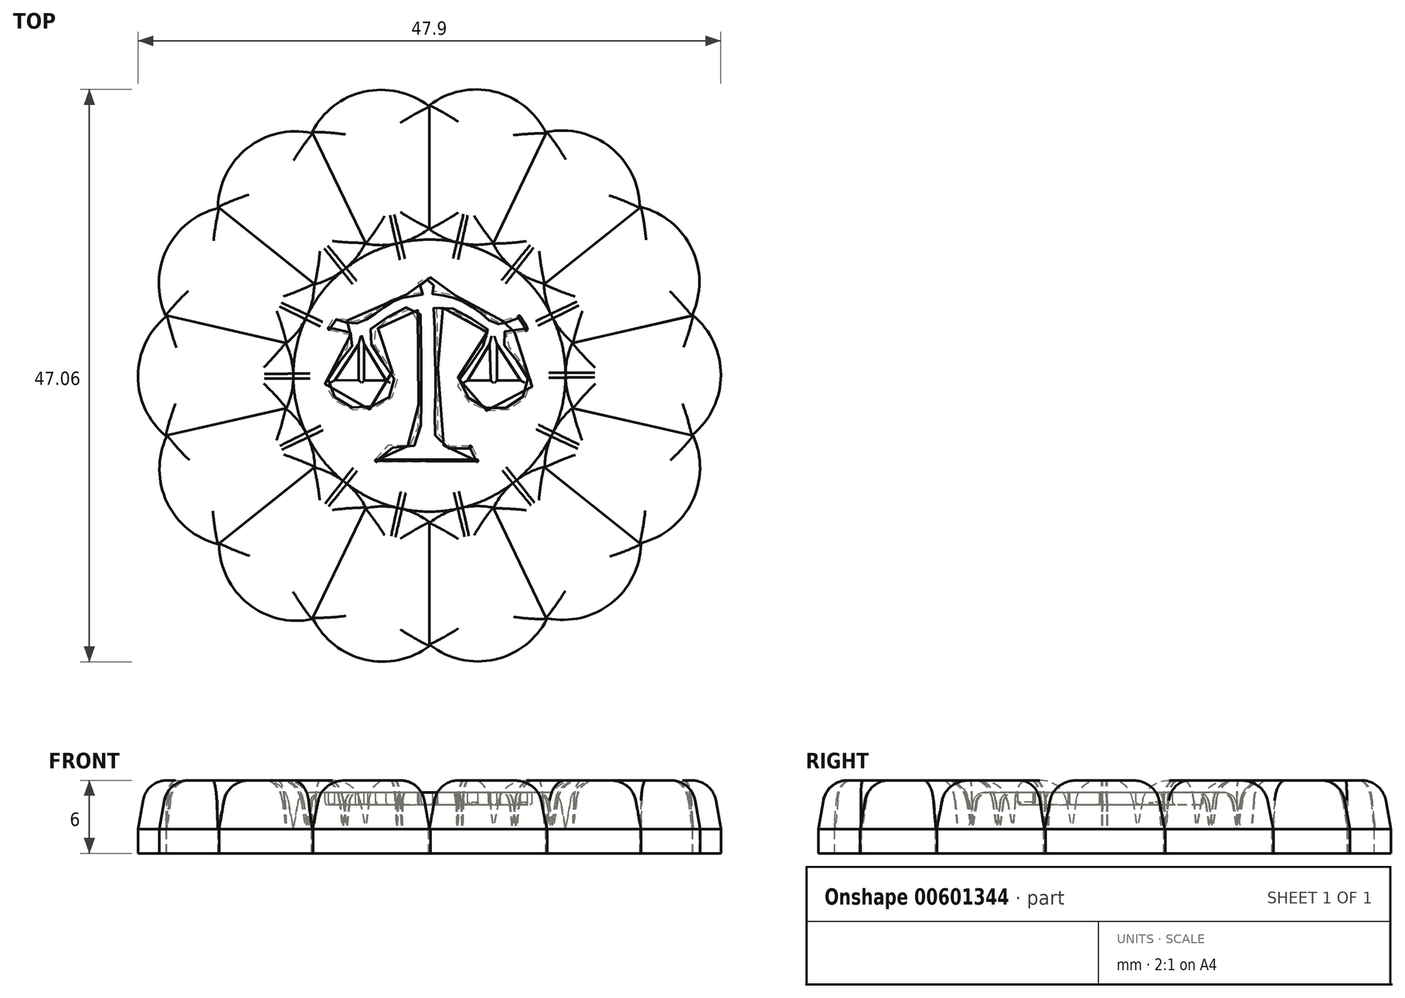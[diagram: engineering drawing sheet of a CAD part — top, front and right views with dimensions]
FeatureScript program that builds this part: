
annotation { "Feature Type Name" : "Feature", "Feature Type Description" : "" }
export const myFeature = defineFeature(function(context is Context, id is Id, definition is map)
    precondition{}
    {
        {
            var Q0;
            Q0=qCreatedBy(makeId("Top.planeOp"),FACE);
            var sketch = newSketch(context, id + "F0", { "sketchPlane" : qUnion([Q0])});
            skCircle(sketch, "E0", {"center": v(0, 0) * mm, "radius": 11.19 * mm});
            skLineSegment(sketch, "E1", {"start": v(0, 11.19) * mm, "end": v(0, 22.24) * mm});
            skLineSegment(sketch, "E2", {"start": v(4.86, 10.08) * mm, "end": v(9.6, 19.92) * mm});
            skArc(sketch, "E3", {"start": v(-0.04, 12.08) * mm, "mid": v(2.48, 10.9) * mm, "end": v(5.26, 10.91) * mm});
            skPoint(sketch, "E3.third.point", {"position": v(2.25, 10.96) * mm});
            skArc(sketch, "E4.1.0", {"start": v(-5.28, 10.86) * mm, "mid": v(-2.5, 10.9) * mm, "end": v(0, 12.11) * mm});
            skLineSegment(sketch, "E4.1.1", {"start": v(0, 11.19) * mm, "end": v(0, 22.11) * mm});
            skLineSegment(sketch, "E4.1.2", {"start": v(-4.85, 10.08) * mm, "end": v(-9.65, 20.03) * mm});
            skArc(sketch, "E4.2.0", {"start": v(-9.6, 19.92) * mm, "mid": v(-14.96, 18.7) * mm, "end": v(-17.39, 13.76) * mm});
            skLineSegment(sketch, "E4.2.1", {"start": v(-4.85, 10.08) * mm, "end": v(-9.6, 19.92) * mm});
            skLineSegment(sketch, "E4.2.2", {"start": v(-8.75, 6.98) * mm, "end": v(-17.39, 13.86) * mm});
            skArc(sketch, "E4.3.0", {"start": v(-11.79, 2.65) * mm, "mid": v(-10.08, 4.84) * mm, "end": v(-9.47, 7.55) * mm});
            skLineSegment(sketch, "E4.3.1", {"start": v(-8.75, 6.98) * mm, "end": v(-17.29, 13.79) * mm});
            skLineSegment(sketch, "E4.3.2", {"start": v(-10.9, 2.49) * mm, "end": v(-21.68, 4.95) * mm});
            skArc(sketch, "E4.4.0", {"start": v(-11.77, -2.73) * mm, "mid": v(-11.18, -0.01) * mm, "end": v(-11.81, 2.7) * mm});
            skLineSegment(sketch, "E4.4.1", {"start": v(-10.9, 2.5) * mm, "end": v(-21.56, 4.92) * mm});
            skLineSegment(sketch, "E4.4.2", {"start": v(-10.9, -2.49) * mm, "end": v(-21.68, -4.95) * mm});
            skArc(sketch, "E4.5.0", {"start": v(-9.42, -7.57) * mm, "mid": v(-10.07, -4.86) * mm, "end": v(-11.81, -2.7) * mm});
            skLineSegment(sketch, "E4.5.1", {"start": v(-10.9, -2.49) * mm, "end": v(-21.56, -4.92) * mm});
            skLineSegment(sketch, "E4.5.2", {"start": v(-8.75, -6.98) * mm, "end": v(-17.39, -13.86) * mm});
            skArc(sketch, "E4.6.0", {"start": v(-5.2, -10.9) * mm, "mid": v(-6.96, -8.75) * mm, "end": v(-9.47, -7.55) * mm});
            skLineSegment(sketch, "E4.6.1", {"start": v(-8.75, -6.97) * mm, "end": v(-17.29, -13.78) * mm});
            skLineSegment(sketch, "E4.6.2", {"start": v(-4.85, -10.08) * mm, "end": v(-9.65, -20.03) * mm});
            skArc(sketch, "E4.7.0", {"start": v(0.04, -12.08) * mm, "mid": v(-2.48, -10.9) * mm, "end": v(-5.26, -10.91) * mm});
            skLineSegment(sketch, "E4.7.1", {"start": v(-4.86, -10.08) * mm, "end": v(-9.6, -19.92) * mm});
            skLineSegment(sketch, "E4.7.2", {"start": v(0, -11.19) * mm, "end": v(0, -22.24) * mm});
            skArc(sketch, "E4.8.0", {"start": v(5.28, -10.86) * mm, "mid": v(2.5, -10.9) * mm, "end": v(0, -12.11) * mm});
            skLineSegment(sketch, "E4.8.1", {"start": v(0, -11.19) * mm, "end": v(0, -22.11) * mm});
            skLineSegment(sketch, "E4.8.2", {"start": v(4.85, -10.08) * mm, "end": v(9.65, -20.03) * mm});
            skArc(sketch, "E4.9.0", {"start": v(9.47, -7.5) * mm, "mid": v(6.98, -8.74) * mm, "end": v(5.26, -10.92) * mm});
            skLineSegment(sketch, "E4.9.1", {"start": v(4.85, -10.08) * mm, "end": v(9.6, -19.92) * mm});
            skLineSegment(sketch, "E4.9.2", {"start": v(9.42, -7.51) * mm, "end": v(17.39, -13.86) * mm});
            skArc(sketch, "E4.10.0", {"start": v(11.79, -2.65) * mm, "mid": v(10.08, -4.84) * mm, "end": v(9.47, -7.55) * mm});
            skLineSegment(sketch, "E4.10.1", {"start": v(8.75, -6.98) * mm, "end": v(17.29, -13.79) * mm});
            skLineSegment(sketch, "E4.10.2", {"start": v(10.9, -2.49) * mm, "end": v(21.68, -4.95) * mm});
            skArc(sketch, "E4.11.0", {"start": v(11.77, 2.73) * mm, "mid": v(11.18, 0.01) * mm, "end": v(11.81, -2.7) * mm});
            skLineSegment(sketch, "E4.11.1", {"start": v(10.9, -2.5) * mm, "end": v(21.56, -4.92) * mm});
            skLineSegment(sketch, "E4.11.2", {"start": v(10.9, 2.49) * mm, "end": v(21.68, 4.95) * mm});
            skArc(sketch, "E4.12.0", {"start": v(9.42, 7.57) * mm, "mid": v(10.07, 4.86) * mm, "end": v(11.81, 2.7) * mm});
            skLineSegment(sketch, "E4.12.1", {"start": v(10.9, 2.49) * mm, "end": v(21.56, 4.92) * mm});
            skLineSegment(sketch, "E4.12.2", {"start": v(8.75, 6.98) * mm, "end": v(17.39, 13.86) * mm});
            skArc(sketch, "E4.13.0", {"start": v(5.2, 10.9) * mm, "mid": v(6.96, 8.75) * mm, "end": v(9.47, 7.55) * mm});
            skLineSegment(sketch, "E4.13.1", {"start": v(8.75, 6.97) * mm, "end": v(17.29, 13.78) * mm});
            skLineSegment(sketch, "E4.13.2", {"start": v(4.85, 10.08) * mm, "end": v(9.65, 20.03) * mm});
            skArc(sketch, "E5.trimOffspring", {"start": v(0, 22.11) * mm, "mid": v(-5.36, 23.34) * mm, "end": v(-9.7, 19.95) * mm});
            skArc(sketch, "E6.trimOffspring", {"start": v(9.6, 19.92) * mm, "mid": v(5.3, 23.36) * mm, "end": v(-0.08, 22.18) * mm});
            skArc(sketch, "E7.trimOffspring", {"start": v(17.29, 13.78) * mm, "mid": v(14.9, 18.75) * mm, "end": v(9.55, 20.01) * mm});
            skArc(sketch, "E8.trimOffspring", {"start": v(21.56, 4.92) * mm, "mid": v(21.57, 10.42) * mm, "end": v(17.29, 13.89) * mm});
            skArc(sketch, "E9.trimOffspring", {"start": v(21.56, -4.92) * mm, "mid": v(23.95, 0.03) * mm, "end": v(21.6, 5.01) * mm});
            skArc(sketch, "E10.trimOffspring", {"start": v(17.29, -13.79) * mm, "mid": v(21.6, -10.36) * mm, "end": v(21.64, -4.86) * mm});
            skArc(sketch, "E11.trimOffspring", {"start": v(9.6, -19.92) * mm, "mid": v(14.96, -18.7) * mm, "end": v(17.39, -13.76) * mm});
            skArc(sketch, "E12.trimOffspring", {"start": v(0, -22.11) * mm, "mid": v(5.36, -23.34) * mm, "end": v(9.7, -19.95) * mm});
            skArc(sketch, "E13.trimOffspring", {"start": v(-9.6, -19.92) * mm, "mid": v(-5.3, -23.36) * mm, "end": v(0.08, -22.18) * mm});
            skArc(sketch, "E14.trimOffspring", {"start": v(-17.29, -13.78) * mm, "mid": v(-14.9, -18.75) * mm, "end": v(-9.55, -20.01) * mm});
            skArc(sketch, "E15.trimOffspring", {"start": v(-21.56, -4.92) * mm, "mid": v(-21.57, -10.42) * mm, "end": v(-17.29, -13.89) * mm});
            skArc(sketch, "E16.trimOffspring", {"start": v(-21.56, 4.92) * mm, "mid": v(-23.95, -0.03) * mm, "end": v(-21.6, -5.01) * mm});
            skArc(sketch, "E17.trimOffspring", {"start": v(-9.47, 7.5) * mm, "mid": v(-6.98, 8.74) * mm, "end": v(-5.26, 10.92) * mm});
            skArc(sketch, "E18.trimOffspring", {"start": v(-17.29, 13.79) * mm, "mid": v(-21.6, 10.36) * mm, "end": v(-21.64, 4.86) * mm});
            skSolve(sketch);
        }
        {
            var Q0;
            {var subQ0=sQuery(id+"F0.wireOp",EDGE,"E17.trimOffspring");var subQ2=sQuery(id+"F0.wireOp",EDGE,"E0");var subQ3=makeQuery(id+"F0.imprint","INTERSECT",VERTEX,{"disambiguationData":[OD(0.0)],"derivedFrom":[subQ2,subQ0]});Q0=makeQuery(id+"F0.imprint","IMPRINT",FACE,{"disambiguationData":[TD([[makeQuery(id+"F0.imprint","IMPRINT",EDGE,{"disambiguationData":[TD([[subQ3,-1.0]])],"derivedFrom":subQ2}),-1.0]])]});}
            var Q1;
            {var subQ4=sQuery(id+"F0.wireOp",EDGE,"E4.1.0");var subQ15=sQuery(id+"F0.wireOp",EDGE,"E0");var subQ16=makeQuery(id+"F0.imprint","INTERSECT",VERTEX,{"disambiguationData":[OD(0.0)],"derivedFrom":[subQ15,subQ4]});Q1=makeQuery(id+"F0.imprint","IMPRINT",FACE,{"disambiguationData":[TD([[makeQuery(id+"F0.imprint","IMPRINT",EDGE,{"disambiguationData":[TD([[subQ16,-1.0]])],"derivedFrom":subQ15}),-1.0]])]});}
            var Q2;
            {var subQ10=sQuery(id+"F0.wireOp",EDGE,"E3");var subQ14=sQuery(id+"F0.wireOp",EDGE,"E0");var subQ15=makeQuery(id+"F0.imprint","INTERSECT",VERTEX,{"disambiguationData":[OD(0.0)],"derivedFrom":[subQ14,subQ10]});Q2=makeQuery(id+"F0.imprint","IMPRINT",FACE,{"disambiguationData":[TD([[makeQuery(id+"F0.imprint","IMPRINT",EDGE,{"disambiguationData":[TD([[subQ15,-1.0]])],"derivedFrom":subQ14}),-1.0]])]});}
            var Q3;
            {var subQ10=sQuery(id+"F0.wireOp",EDGE,"E4.13.0");var subQ11=sQuery(id+"F0.wireOp",EDGE,"E0");var subQ16=makeQuery(id+"F0.imprint","INTERSECT",VERTEX,{"disambiguationData":[OD(0.0)],"derivedFrom":[subQ11,subQ10]});Q3=makeQuery(id+"F0.imprint","IMPRINT",FACE,{"disambiguationData":[TD([[makeQuery(id+"F0.imprint","IMPRINT",EDGE,{"disambiguationData":[TD([[subQ16,-1.0]])],"derivedFrom":subQ11}),-1.0]])]});}
            var Q4;
            {var subQ11=sQuery(id+"F0.wireOp",EDGE,"E4.12.0");var subQ15=sQuery(id+"F0.wireOp",EDGE,"E0");var subQ16=makeQuery(id+"F0.imprint","INTERSECT",VERTEX,{"disambiguationData":[OD(0.0)],"derivedFrom":[subQ15,subQ11]});Q4=makeQuery(id+"F0.imprint","IMPRINT",FACE,{"disambiguationData":[TD([[makeQuery(id+"F0.imprint","IMPRINT",EDGE,{"disambiguationData":[TD([[subQ16,-1.0]])],"derivedFrom":subQ15}),-1.0]])]});}
            var Q5;
            {var subQ6=sQuery(id+"F0.wireOp",EDGE,"E4.11.0");var subQ11=sQuery(id+"F0.wireOp",EDGE,"E0");var subQ12=makeQuery(id+"F0.imprint","INTERSECT",VERTEX,{"disambiguationData":[OD(0.0)],"derivedFrom":[subQ11,subQ6]});Q5=makeQuery(id+"F0.imprint","IMPRINT",FACE,{"disambiguationData":[TD([[makeQuery(id+"F0.imprint","IMPRINT",EDGE,{"disambiguationData":[TD([[subQ12,1.0]])],"derivedFrom":subQ11}),-1.0]])]});}
            var Q6;
            {var subQ10=sQuery(id+"F0.wireOp",EDGE,"E4.10.0");var subQ14=sQuery(id+"F0.wireOp",EDGE,"E0");var subQ15=makeQuery(id+"F0.imprint","INTERSECT",VERTEX,{"disambiguationData":[OD(0.0)],"derivedFrom":[subQ14,subQ10]});Q6=makeQuery(id+"F0.imprint","IMPRINT",FACE,{"disambiguationData":[TD([[makeQuery(id+"F0.imprint","IMPRINT",EDGE,{"disambiguationData":[TD([[subQ15,-1.0]])],"derivedFrom":subQ14}),-1.0]])]});}
            var Q7;
            {var subQ4=sQuery(id+"F0.wireOp",EDGE,"E4.9.0");var subQ5=sQuery(id+"F0.wireOp",EDGE,"E0");var subQ17=makeQuery(id+"F0.imprint","INTERSECT",VERTEX,{"disambiguationData":[OD(0.0)],"derivedFrom":[subQ5,subQ4]});Q7=makeQuery(id+"F0.imprint","IMPRINT",FACE,{"disambiguationData":[TD([[makeQuery(id+"F0.imprint","IMPRINT",EDGE,{"disambiguationData":[TD([[subQ17,-1.0]])],"derivedFrom":subQ5}),-1.0]])]});}
            var Q8;
            {var subQ6=sQuery(id+"F0.wireOp",EDGE,"E4.8.0");var subQ11=sQuery(id+"F0.wireOp",EDGE,"E0");var subQ12=makeQuery(id+"F0.imprint","INTERSECT",VERTEX,{"disambiguationData":[OD(0.0)],"derivedFrom":[subQ11,subQ6]});Q8=makeQuery(id+"F0.imprint","IMPRINT",FACE,{"disambiguationData":[TD([[makeQuery(id+"F0.imprint","IMPRINT",EDGE,{"disambiguationData":[TD([[subQ12,-1.0]])],"derivedFrom":subQ11}),-1.0]])]});}
            var Q9;
            {var subQ4=sQuery(id+"F0.wireOp",EDGE,"E4.7.0");var subQ9=sQuery(id+"F0.wireOp",EDGE,"E0");var subQ10=makeQuery(id+"F0.imprint","INTERSECT",VERTEX,{"disambiguationData":[OD(0.0)],"derivedFrom":[subQ9,subQ4]});Q9=makeQuery(id+"F0.imprint","IMPRINT",FACE,{"disambiguationData":[TD([[makeQuery(id+"F0.imprint","IMPRINT",EDGE,{"disambiguationData":[TD([[subQ10,-1.0]])],"derivedFrom":subQ9}),-1.0]])]});}
            var Q10;
            {var subQ6=sQuery(id+"F0.wireOp",EDGE,"E4.6.0");var subQ14=sQuery(id+"F0.wireOp",EDGE,"E0");var subQ15=makeQuery(id+"F0.imprint","INTERSECT",VERTEX,{"disambiguationData":[OD(0.0)],"derivedFrom":[subQ14,subQ6]});Q10=makeQuery(id+"F0.imprint","IMPRINT",FACE,{"disambiguationData":[TD([[makeQuery(id+"F0.imprint","IMPRINT",EDGE,{"disambiguationData":[TD([[subQ15,-1.0]])],"derivedFrom":subQ14}),-1.0]])]});}
            var Q11;
            {var subQ10=sQuery(id+"F0.wireOp",EDGE,"E4.5.0");var subQ14=sQuery(id+"F0.wireOp",EDGE,"E0");var subQ15=makeQuery(id+"F0.imprint","INTERSECT",VERTEX,{"disambiguationData":[OD(0.0)],"derivedFrom":[subQ14,subQ10]});Q11=makeQuery(id+"F0.imprint","IMPRINT",FACE,{"disambiguationData":[TD([[makeQuery(id+"F0.imprint","IMPRINT",EDGE,{"disambiguationData":[TD([[subQ15,-1.0]])],"derivedFrom":subQ14}),-1.0]])]});}
            var Q12;
            {var subQ10=sQuery(id+"F0.wireOp",EDGE,"E4.4.0");var subQ14=sQuery(id+"F0.wireOp",EDGE,"E0");var subQ15=makeQuery(id+"F0.imprint","INTERSECT",VERTEX,{"disambiguationData":[OD(0.0)],"derivedFrom":[subQ14,subQ10]});Q12=makeQuery(id+"F0.imprint","IMPRINT",FACE,{"disambiguationData":[TD([[makeQuery(id+"F0.imprint","IMPRINT",EDGE,{"disambiguationData":[TD([[subQ15,-1.0]])],"derivedFrom":subQ14}),-1.0]])]});}
            var Q13;
            {var subQ11=sQuery(id+"F0.wireOp",EDGE,"E4.3.0");var subQ12=sQuery(id+"F0.wireOp",EDGE,"E0");var subQ17=makeQuery(id+"F0.imprint","INTERSECT",VERTEX,{"disambiguationData":[OD(0.0)],"derivedFrom":[subQ12,subQ11]});Q13=makeQuery(id+"F0.imprint","IMPRINT",FACE,{"disambiguationData":[TD([[makeQuery(id+"F0.imprint","IMPRINT",EDGE,{"disambiguationData":[TD([[subQ17,-1.0]])],"derivedFrom":subQ12}),-1.0]])]});}
            extrude(context, id + "F1", {"entities" : qUnion([Q0, Q1, Q2, Q3, Q4, Q5, Q6, Q7, Q8, Q9, Q10, Q11, Q12, Q13]), "depth" : 4 * mm, "offsetDistance" : 25 * mm, "hasDraft" : true, "draftAngle" : 10 * degree, "draftPullDirection" : true});
        }
        {
            var Q0;
            {var subQ1=sQuery(id+"F0.wireOp",EDGE,"E0");var subQ13=makeQuery(id+"F0.imprint","INTERSECT",VERTEX,{"derivedFrom":[subQ1,sQuery(id+"F0.wireOp",EDGE,"E4.12.1")]});Q0=makeQuery(id+"F0.imprint","IMPRINT",FACE,{"disambiguationData":[TD([[makeQuery(id+"F0.imprint","IMPRINT",EDGE,{"disambiguationData":[TD([[subQ13,1.0]])],"derivedFrom":subQ1}),1.0]])]});}
            extrude(context, id + "F2", {"entities" : qUnion([Q0]), "depth" : 3 * mm, "offsetDistance" : 25 * mm, "hasDraft" : true, "draftAngle" : 10 * degree, "draftPullDirection" : true});
        }
        {
            var Q0;
            {var subQ10=sQuery(id+"F0.wireOp",EDGE,"E4.5.0");var subQ14=sQuery(id+"F0.wireOp",EDGE,"E0");var subQ15=makeQuery(id+"F0.imprint","INTERSECT",VERTEX,{"disambiguationData":[OD(0.0)],"derivedFrom":[subQ14,subQ10]});Q0=makeQuery(id+"F0.imprint","IMPRINT",FACE,{"disambiguationData":[TD([[makeQuery(id+"F0.imprint","IMPRINT",EDGE,{"disambiguationData":[TD([[subQ15,-1.0]])],"derivedFrom":subQ14}),-1.0]])]});}
            var Q1;
            {var subQ6=sQuery(id+"F0.wireOp",EDGE,"E4.11.0");var subQ11=sQuery(id+"F0.wireOp",EDGE,"E0");var subQ12=makeQuery(id+"F0.imprint","INTERSECT",VERTEX,{"disambiguationData":[OD(0.0)],"derivedFrom":[subQ11,subQ6]});Q1=makeQuery(id+"F0.imprint","IMPRINT",FACE,{"disambiguationData":[TD([[makeQuery(id+"F0.imprint","IMPRINT",EDGE,{"disambiguationData":[TD([[subQ12,1.0]])],"derivedFrom":subQ11}),-1.0]])]});}
            var Q2;
            {var subQ10=sQuery(id+"F0.wireOp",EDGE,"E4.10.0");var subQ14=sQuery(id+"F0.wireOp",EDGE,"E0");var subQ15=makeQuery(id+"F0.imprint","INTERSECT",VERTEX,{"disambiguationData":[OD(0.0)],"derivedFrom":[subQ14,subQ10]});Q2=makeQuery(id+"F0.imprint","IMPRINT",FACE,{"disambiguationData":[TD([[makeQuery(id+"F0.imprint","IMPRINT",EDGE,{"disambiguationData":[TD([[subQ15,-1.0]])],"derivedFrom":subQ14}),-1.0]])]});}
            var Q3;
            {var subQ10=sQuery(id+"F0.wireOp",EDGE,"E4.4.0");var subQ14=sQuery(id+"F0.wireOp",EDGE,"E0");var subQ15=makeQuery(id+"F0.imprint","INTERSECT",VERTEX,{"disambiguationData":[OD(0.0)],"derivedFrom":[subQ14,subQ10]});Q3=makeQuery(id+"F0.imprint","IMPRINT",FACE,{"disambiguationData":[TD([[makeQuery(id+"F0.imprint","IMPRINT",EDGE,{"disambiguationData":[TD([[subQ15,-1.0]])],"derivedFrom":subQ14}),-1.0]])]});}
            var Q4;
            {var subQ11=sQuery(id+"F0.wireOp",EDGE,"E4.3.0");var subQ12=sQuery(id+"F0.wireOp",EDGE,"E0");var subQ17=makeQuery(id+"F0.imprint","INTERSECT",VERTEX,{"disambiguationData":[OD(0.0)],"derivedFrom":[subQ12,subQ11]});Q4=makeQuery(id+"F0.imprint","IMPRINT",FACE,{"disambiguationData":[TD([[makeQuery(id+"F0.imprint","IMPRINT",EDGE,{"disambiguationData":[TD([[subQ17,-1.0]])],"derivedFrom":subQ12}),-1.0]])]});}
            var Q5;
            {var subQ1=sQuery(id+"F0.wireOp",EDGE,"E0");var subQ13=makeQuery(id+"F0.imprint","INTERSECT",VERTEX,{"derivedFrom":[subQ1,sQuery(id+"F0.wireOp",EDGE,"E4.12.1")]});Q5=makeQuery(id+"F0.imprint","IMPRINT",FACE,{"disambiguationData":[TD([[makeQuery(id+"F0.imprint","IMPRINT",EDGE,{"disambiguationData":[TD([[subQ13,1.0]])],"derivedFrom":subQ1}),1.0]])]});}
            var Q6;
            {var subQ4=sQuery(id+"F0.wireOp",EDGE,"E4.9.0");var subQ5=sQuery(id+"F0.wireOp",EDGE,"E0");var subQ17=makeQuery(id+"F0.imprint","INTERSECT",VERTEX,{"disambiguationData":[OD(0.0)],"derivedFrom":[subQ5,subQ4]});Q6=makeQuery(id+"F0.imprint","IMPRINT",FACE,{"disambiguationData":[TD([[makeQuery(id+"F0.imprint","IMPRINT",EDGE,{"disambiguationData":[TD([[subQ17,-1.0]])],"derivedFrom":subQ5}),-1.0]])]});}
            var Q7;
            {var subQ0=sQuery(id+"F0.wireOp",EDGE,"E17.trimOffspring");var subQ2=sQuery(id+"F0.wireOp",EDGE,"E0");var subQ3=makeQuery(id+"F0.imprint","INTERSECT",VERTEX,{"disambiguationData":[OD(0.0)],"derivedFrom":[subQ2,subQ0]});Q7=makeQuery(id+"F0.imprint","IMPRINT",FACE,{"disambiguationData":[TD([[makeQuery(id+"F0.imprint","IMPRINT",EDGE,{"disambiguationData":[TD([[subQ3,-1.0]])],"derivedFrom":subQ2}),-1.0]])]});}
            var Q8;
            {var subQ10=sQuery(id+"F0.wireOp",EDGE,"E4.13.0");var subQ11=sQuery(id+"F0.wireOp",EDGE,"E0");var subQ16=makeQuery(id+"F0.imprint","INTERSECT",VERTEX,{"disambiguationData":[OD(0.0)],"derivedFrom":[subQ11,subQ10]});Q8=makeQuery(id+"F0.imprint","IMPRINT",FACE,{"disambiguationData":[TD([[makeQuery(id+"F0.imprint","IMPRINT",EDGE,{"disambiguationData":[TD([[subQ16,-1.0]])],"derivedFrom":subQ11}),-1.0]])]});}
            var Q9;
            {var subQ6=sQuery(id+"F0.wireOp",EDGE,"E4.6.0");var subQ14=sQuery(id+"F0.wireOp",EDGE,"E0");var subQ15=makeQuery(id+"F0.imprint","INTERSECT",VERTEX,{"disambiguationData":[OD(0.0)],"derivedFrom":[subQ14,subQ6]});Q9=makeQuery(id+"F0.imprint","IMPRINT",FACE,{"disambiguationData":[TD([[makeQuery(id+"F0.imprint","IMPRINT",EDGE,{"disambiguationData":[TD([[subQ15,-1.0]])],"derivedFrom":subQ14}),-1.0]])]});}
            var Q10;
            {var subQ10=sQuery(id+"F0.wireOp",EDGE,"E3");var subQ14=sQuery(id+"F0.wireOp",EDGE,"E0");var subQ15=makeQuery(id+"F0.imprint","INTERSECT",VERTEX,{"disambiguationData":[OD(0.0)],"derivedFrom":[subQ14,subQ10]});Q10=makeQuery(id+"F0.imprint","IMPRINT",FACE,{"disambiguationData":[TD([[makeQuery(id+"F0.imprint","IMPRINT",EDGE,{"disambiguationData":[TD([[subQ15,-1.0]])],"derivedFrom":subQ14}),-1.0]])]});}
            var Q11;
            {var subQ4=sQuery(id+"F0.wireOp",EDGE,"E4.7.0");var subQ9=sQuery(id+"F0.wireOp",EDGE,"E0");var subQ10=makeQuery(id+"F0.imprint","INTERSECT",VERTEX,{"disambiguationData":[OD(0.0)],"derivedFrom":[subQ9,subQ4]});Q11=makeQuery(id+"F0.imprint","IMPRINT",FACE,{"disambiguationData":[TD([[makeQuery(id+"F0.imprint","IMPRINT",EDGE,{"disambiguationData":[TD([[subQ10,-1.0]])],"derivedFrom":subQ9}),-1.0]])]});}
            var Q12;
            {var subQ4=sQuery(id+"F0.wireOp",EDGE,"E4.1.0");var subQ15=sQuery(id+"F0.wireOp",EDGE,"E0");var subQ16=makeQuery(id+"F0.imprint","INTERSECT",VERTEX,{"disambiguationData":[OD(0.0)],"derivedFrom":[subQ15,subQ4]});Q12=makeQuery(id+"F0.imprint","IMPRINT",FACE,{"disambiguationData":[TD([[makeQuery(id+"F0.imprint","IMPRINT",EDGE,{"disambiguationData":[TD([[subQ16,-1.0]])],"derivedFrom":subQ15}),-1.0]])]});}
            var Q13;
            {var subQ6=sQuery(id+"F0.wireOp",EDGE,"E4.8.0");var subQ11=sQuery(id+"F0.wireOp",EDGE,"E0");var subQ12=makeQuery(id+"F0.imprint","INTERSECT",VERTEX,{"disambiguationData":[OD(0.0)],"derivedFrom":[subQ11,subQ6]});Q13=makeQuery(id+"F0.imprint","IMPRINT",FACE,{"disambiguationData":[TD([[makeQuery(id+"F0.imprint","IMPRINT",EDGE,{"disambiguationData":[TD([[subQ12,-1.0]])],"derivedFrom":subQ11}),-1.0]])]});}
            var Q14;
            {var subQ11=sQuery(id+"F0.wireOp",EDGE,"E4.12.0");var subQ15=sQuery(id+"F0.wireOp",EDGE,"E0");var subQ16=makeQuery(id+"F0.imprint","INTERSECT",VERTEX,{"disambiguationData":[OD(0.0)],"derivedFrom":[subQ15,subQ11]});Q14=makeQuery(id+"F0.imprint","IMPRINT",FACE,{"disambiguationData":[TD([[makeQuery(id+"F0.imprint","IMPRINT",EDGE,{"disambiguationData":[TD([[subQ16,-1.0]])],"derivedFrom":subQ15}),-1.0]])]});}
            var Q15;
            {var subQ0=sQuery(id+"F0.wireOp",EDGE,"E4.11.0");var subQ1=sQuery(id+"F0.wireOp",EDGE,"E0");var subQ2=makeQuery(id+"F0.imprint","INTERSECT",VERTEX,{"disambiguationData":[OD(0.0)],"derivedFrom":[subQ1,subQ0]});Q15=makeQuery(id+"F0.imprint","IMPRINT",FACE,{"disambiguationData":[TD([[makeQuery(id+"F0.imprint","IMPRINT",EDGE,{"disambiguationData":[TD([[subQ2,1.0]])],"derivedFrom":subQ1}),1.0]])]});}
            var Q16;
            {var subQ0=sQuery(id+"F0.wireOp",EDGE,"E4.8.1");var subQ1=sQuery(id+"F0.wireOp",EDGE,"E0");var subQ2=makeQuery(id+"F0.imprint","INTERSECT",VERTEX,{"derivedFrom":[subQ1,subQ0]});Q16=makeQuery(id+"F0.imprint","IMPRINT",FACE,{"disambiguationData":[TD([[makeQuery(id+"F0.imprint","IMPRINT",EDGE,{"disambiguationData":[TD([[subQ2,1.0]])],"derivedFrom":subQ1}),-1.0]])]});}
            var Q17;
            {var subQ0=sQuery(id+"F0.wireOp",EDGE,"E4.7.1");var subQ1=sQuery(id+"F0.wireOp",EDGE,"E0");var subQ2=makeQuery(id+"F0.imprint","INTERSECT",VERTEX,{"derivedFrom":[subQ1,subQ0]});Q17=makeQuery(id+"F0.imprint","IMPRINT",FACE,{"disambiguationData":[TD([[makeQuery(id+"F0.imprint","IMPRINT",EDGE,{"disambiguationData":[TD([[subQ2,1.0]])],"derivedFrom":subQ1}),-1.0]])]});}
            var Q18;
            {var subQ0=sQuery(id+"F0.wireOp",EDGE,"E4.13.2");var subQ1=sQuery(id+"F0.wireOp",EDGE,"E0");var subQ2=makeQuery(id+"F0.imprint","INTERSECT",VERTEX,{"derivedFrom":[subQ1,subQ0]});Q18=makeQuery(id+"F0.imprint","IMPRINT",FACE,{"disambiguationData":[TD([[makeQuery(id+"F0.imprint","IMPRINT",EDGE,{"disambiguationData":[TD([[subQ2,-1.0]])],"derivedFrom":subQ1}),-1.0]])]});}
            var Q19;
            {var subQ0=sQuery(id+"F0.wireOp",EDGE,"E4.7.2");var subQ1=sQuery(id+"F0.wireOp",EDGE,"E0");var subQ2=makeQuery(id+"F0.imprint","INTERSECT",VERTEX,{"derivedFrom":[subQ1,subQ0]});Q19=makeQuery(id+"F0.imprint","IMPRINT",FACE,{"disambiguationData":[TD([[makeQuery(id+"F0.imprint","IMPRINT",EDGE,{"disambiguationData":[TD([[subQ2,-1.0]])],"derivedFrom":subQ1}),-1.0]])]});}
            var Q20;
            {var subQ0=sQuery(id+"F0.wireOp",EDGE,"E4.6.1");var subQ1=sQuery(id+"F0.wireOp",EDGE,"E0");var subQ2=makeQuery(id+"F0.imprint","INTERSECT",VERTEX,{"derivedFrom":[subQ1,subQ0]});Q20=makeQuery(id+"F0.imprint","IMPRINT",FACE,{"disambiguationData":[TD([[makeQuery(id+"F0.imprint","IMPRINT",EDGE,{"disambiguationData":[TD([[subQ2,1.0]])],"derivedFrom":subQ1}),-1.0]])]});}
            var Q21;
            {var subQ0=sQuery(id+"F0.wireOp",EDGE,"E1");var subQ1=sQuery(id+"F0.wireOp",EDGE,"E0");var subQ2=makeQuery(id+"F0.imprint","INTERSECT",VERTEX,{"derivedFrom":[subQ1,subQ0]});Q21=makeQuery(id+"F0.imprint","IMPRINT",FACE,{"disambiguationData":[TD([[makeQuery(id+"F0.imprint","IMPRINT",EDGE,{"disambiguationData":[TD([[subQ2,-1.0]])],"derivedFrom":subQ1}),-1.0]])]});}
            var Q22;
            {var subQ0=sQuery(id+"F0.wireOp",EDGE,"E4.12.1");var subQ1=sQuery(id+"F0.wireOp",EDGE,"E0");var subQ2=makeQuery(id+"F0.imprint","INTERSECT",VERTEX,{"derivedFrom":[subQ1,subQ0]});Q22=makeQuery(id+"F0.imprint","IMPRINT",FACE,{"disambiguationData":[TD([[makeQuery(id+"F0.imprint","IMPRINT",EDGE,{"disambiguationData":[TD([[subQ2,1.0]])],"derivedFrom":subQ1}),-1.0]])]});}
            var Q23;
            {var subQ3=sQuery(id+"F0.wireOp",EDGE,"E0");var subQ6=sQuery(id+"F0.wireOp",EDGE,"E4.10.1");var subQ8=makeQuery(id+"F0.imprint","INTERSECT",VERTEX,{"derivedFrom":[subQ3,subQ6]});Q23=makeQuery(id+"F0.imprint","IMPRINT",FACE,{"disambiguationData":[TD([[makeQuery(id+"F0.imprint","IMPRINT",EDGE,{"disambiguationData":[TD([[subQ8,-1.0]])],"derivedFrom":subQ3}),-1.0]])]});}
            var Q24;
            {var subQ0=sQuery(id+"F0.wireOp",EDGE,"E2");var subQ1=sQuery(id+"F0.wireOp",EDGE,"E0");var subQ2=makeQuery(id+"F0.imprint","INTERSECT",VERTEX,{"derivedFrom":[subQ1,subQ0]});Q24=makeQuery(id+"F0.imprint","IMPRINT",FACE,{"disambiguationData":[TD([[makeQuery(id+"F0.imprint","IMPRINT",EDGE,{"disambiguationData":[TD([[subQ2,1.0]])],"derivedFrom":subQ1}),-1.0]])]});}
            var Q25;
            {var subQ0=sQuery(id+"F0.wireOp",EDGE,"E4.4.2");var subQ1=sQuery(id+"F0.wireOp",EDGE,"E0");var subQ2=makeQuery(id+"F0.imprint","INTERSECT",VERTEX,{"derivedFrom":[subQ1,subQ0]});Q25=makeQuery(id+"F0.imprint","IMPRINT",FACE,{"disambiguationData":[TD([[makeQuery(id+"F0.imprint","IMPRINT",EDGE,{"disambiguationData":[TD([[subQ2,-1.0]])],"derivedFrom":subQ1}),-1.0]])]});}
            var Q26;
            {var subQ0=sQuery(id+"F0.wireOp",EDGE,"E4.8.2");var subQ1=sQuery(id+"F0.wireOp",EDGE,"E0");var subQ2=makeQuery(id+"F0.imprint","INTERSECT",VERTEX,{"derivedFrom":[subQ1,subQ0]});Q26=makeQuery(id+"F0.imprint","IMPRINT",FACE,{"disambiguationData":[TD([[makeQuery(id+"F0.imprint","IMPRINT",EDGE,{"disambiguationData":[TD([[subQ2,-1.0]])],"derivedFrom":subQ1}),-1.0]])]});}
            var Q27;
            {var subQ0=sQuery(id+"F0.wireOp",EDGE,"E4.5.1");var subQ1=sQuery(id+"F0.wireOp",EDGE,"E0");var subQ2=makeQuery(id+"F0.imprint","INTERSECT",VERTEX,{"derivedFrom":[subQ1,subQ0]});Q27=makeQuery(id+"F0.imprint","IMPRINT",FACE,{"disambiguationData":[TD([[makeQuery(id+"F0.imprint","IMPRINT",EDGE,{"disambiguationData":[TD([[subQ2,1.0]])],"derivedFrom":subQ1}),-1.0]])]});}
            var Q28;
            {var subQ0=sQuery(id+"F0.wireOp",EDGE,"E4.3.2");var subQ1=sQuery(id+"F0.wireOp",EDGE,"E0");var subQ2=makeQuery(id+"F0.imprint","INTERSECT",VERTEX,{"derivedFrom":[subQ1,subQ0]});Q28=makeQuery(id+"F0.imprint","IMPRINT",FACE,{"disambiguationData":[TD([[makeQuery(id+"F0.imprint","IMPRINT",EDGE,{"disambiguationData":[TD([[subQ2,-1.0]])],"derivedFrom":subQ1}),-1.0]])]});}
            var Q29;
            {var subQ0=sQuery(id+"F0.wireOp",EDGE,"E4.2.1");var subQ1=sQuery(id+"F0.wireOp",EDGE,"E0");var subQ2=makeQuery(id+"F0.imprint","INTERSECT",VERTEX,{"derivedFrom":[subQ1,subQ0]});Q29=makeQuery(id+"F0.imprint","IMPRINT",FACE,{"disambiguationData":[TD([[makeQuery(id+"F0.imprint","IMPRINT",EDGE,{"disambiguationData":[TD([[subQ2,1.0]])],"derivedFrom":subQ1}),-1.0]])]});}
            var Q30;
            {var subQ0=sQuery(id+"F0.wireOp",EDGE,"E4.12.0");var subQ1=sQuery(id+"F0.wireOp",EDGE,"E0");var subQ2=makeQuery(id+"F0.imprint","INTERSECT",VERTEX,{"disambiguationData":[OD(0.0)],"derivedFrom":[subQ1,subQ0]});Q30=makeQuery(id+"F0.imprint","IMPRINT",FACE,{"disambiguationData":[TD([[makeQuery(id+"F0.imprint","IMPRINT",EDGE,{"disambiguationData":[TD([[subQ2,-1.0]])],"derivedFrom":subQ1}),1.0]])]});}
            var Q31;
            {var subQ0=sQuery(id+"F0.wireOp",EDGE,"E4.13.0");var subQ1=sQuery(id+"F0.wireOp",EDGE,"E0");var subQ2=makeQuery(id+"F0.imprint","INTERSECT",VERTEX,{"disambiguationData":[OD(0.0)],"derivedFrom":[subQ1,subQ0]});Q31=makeQuery(id+"F0.imprint","IMPRINT",FACE,{"disambiguationData":[TD([[makeQuery(id+"F0.imprint","IMPRINT",EDGE,{"disambiguationData":[TD([[subQ2,-1.0]])],"derivedFrom":subQ1}),1.0]])]});}
            var Q32;
            {var subQ0=sQuery(id+"F0.wireOp",EDGE,"E4.1.0");var subQ1=sQuery(id+"F0.wireOp",EDGE,"E0");var subQ2=makeQuery(id+"F0.imprint","INTERSECT",VERTEX,{"disambiguationData":[OD(0.0)],"derivedFrom":[subQ1,subQ0]});Q32=makeQuery(id+"F0.imprint","IMPRINT",FACE,{"disambiguationData":[TD([[makeQuery(id+"F0.imprint","IMPRINT",EDGE,{"disambiguationData":[TD([[subQ2,-1.0]])],"derivedFrom":subQ1}),1.0]])]});}
            var Q33;
            {var subQ0=sQuery(id+"F0.wireOp",EDGE,"E4.3.0");var subQ1=sQuery(id+"F0.wireOp",EDGE,"E0");var subQ2=makeQuery(id+"F0.imprint","INTERSECT",VERTEX,{"disambiguationData":[OD(0.0)],"derivedFrom":[subQ1,subQ0]});Q33=makeQuery(id+"F0.imprint","IMPRINT",FACE,{"disambiguationData":[TD([[makeQuery(id+"F0.imprint","IMPRINT",EDGE,{"disambiguationData":[TD([[subQ2,-1.0]])],"derivedFrom":subQ1}),1.0]])]});}
            var Q34;
            {var subQ0=sQuery(id+"F0.wireOp",EDGE,"E4.7.0");var subQ1=sQuery(id+"F0.wireOp",EDGE,"E0");var subQ2=makeQuery(id+"F0.imprint","INTERSECT",VERTEX,{"disambiguationData":[OD(0.0)],"derivedFrom":[subQ1,subQ0]});Q34=makeQuery(id+"F0.imprint","IMPRINT",FACE,{"disambiguationData":[TD([[makeQuery(id+"F0.imprint","IMPRINT",EDGE,{"disambiguationData":[TD([[subQ2,-1.0]])],"derivedFrom":subQ1}),1.0]])]});}
            var Q35;
            {var subQ0=sQuery(id+"F0.wireOp",EDGE,"E4.8.0");var subQ1=sQuery(id+"F0.wireOp",EDGE,"E0");var subQ2=makeQuery(id+"F0.imprint","INTERSECT",VERTEX,{"disambiguationData":[OD(0.0)],"derivedFrom":[subQ1,subQ0]});Q35=makeQuery(id+"F0.imprint","IMPRINT",FACE,{"disambiguationData":[TD([[makeQuery(id+"F0.imprint","IMPRINT",EDGE,{"disambiguationData":[TD([[subQ2,-1.0]])],"derivedFrom":subQ1}),1.0]])]});}
            var Q36;
            {var subQ0=sQuery(id+"F0.wireOp",EDGE,"E4.9.0");var subQ1=sQuery(id+"F0.wireOp",EDGE,"E0");var subQ2=makeQuery(id+"F0.imprint","INTERSECT",VERTEX,{"disambiguationData":[OD(0.0)],"derivedFrom":[subQ1,subQ0]});Q36=makeQuery(id+"F0.imprint","IMPRINT",FACE,{"disambiguationData":[TD([[makeQuery(id+"F0.imprint","IMPRINT",EDGE,{"disambiguationData":[TD([[subQ2,-1.0]])],"derivedFrom":subQ1}),1.0]])]});}
            var Q37;
            {var subQ0=sQuery(id+"F0.wireOp",EDGE,"E4.10.0");var subQ1=sQuery(id+"F0.wireOp",EDGE,"E0");var subQ2=makeQuery(id+"F0.imprint","INTERSECT",VERTEX,{"disambiguationData":[OD(0.0)],"derivedFrom":[subQ1,subQ0]});Q37=makeQuery(id+"F0.imprint","IMPRINT",FACE,{"disambiguationData":[TD([[makeQuery(id+"F0.imprint","IMPRINT",EDGE,{"disambiguationData":[TD([[subQ2,-1.0]])],"derivedFrom":subQ1}),1.0]])]});}
            var Q38;
            {var subQ0=sQuery(id+"F0.wireOp",EDGE,"E4.9.1");var subQ1=sQuery(id+"F0.wireOp",EDGE,"E0");var subQ2=makeQuery(id+"F0.imprint","INTERSECT",VERTEX,{"derivedFrom":[subQ1,subQ0]});Q38=makeQuery(id+"F0.imprint","IMPRINT",FACE,{"disambiguationData":[TD([[makeQuery(id+"F0.imprint","IMPRINT",EDGE,{"disambiguationData":[TD([[subQ2,1.0]])],"derivedFrom":subQ1}),-1.0]])]});}
            var Q39;
            {var subQ0=sQuery(id+"F0.wireOp",EDGE,"E4.11.2");var subQ1=sQuery(id+"F0.wireOp",EDGE,"E0");var subQ2=makeQuery(id+"F0.imprint","INTERSECT",VERTEX,{"derivedFrom":[subQ1,subQ0]});Q39=makeQuery(id+"F0.imprint","IMPRINT",FACE,{"disambiguationData":[TD([[makeQuery(id+"F0.imprint","IMPRINT",EDGE,{"disambiguationData":[TD([[subQ2,-1.0]])],"derivedFrom":subQ1}),-1.0]])]});}
            var Q40;
            {var subQ0=sQuery(id+"F0.wireOp",EDGE,"E4.2.2");var subQ1=sQuery(id+"F0.wireOp",EDGE,"E0");var subQ2=makeQuery(id+"F0.imprint","INTERSECT",VERTEX,{"derivedFrom":[subQ1,subQ0]});Q40=makeQuery(id+"F0.imprint","IMPRINT",FACE,{"disambiguationData":[TD([[makeQuery(id+"F0.imprint","IMPRINT",EDGE,{"disambiguationData":[TD([[subQ2,-1.0]])],"derivedFrom":subQ1}),-1.0]])]});}
            var Q41;
            {var subQ0=sQuery(id+"F0.wireOp",EDGE,"E4.3.1");var subQ1=sQuery(id+"F0.wireOp",EDGE,"E0");var subQ2=makeQuery(id+"F0.imprint","INTERSECT",VERTEX,{"derivedFrom":[subQ1,subQ0]});Q41=makeQuery(id+"F0.imprint","IMPRINT",FACE,{"disambiguationData":[TD([[makeQuery(id+"F0.imprint","IMPRINT",EDGE,{"disambiguationData":[TD([[subQ2,1.0]])],"derivedFrom":subQ1}),-1.0]])]});}
            var Q42;
            {var subQ0=sQuery(id+"F0.wireOp",EDGE,"E4.10.1");var subQ1=sQuery(id+"F0.wireOp",EDGE,"E0");var subQ2=makeQuery(id+"F0.imprint","INTERSECT",VERTEX,{"derivedFrom":[subQ1,subQ0]});Q42=makeQuery(id+"F0.imprint","IMPRINT",FACE,{"disambiguationData":[TD([[makeQuery(id+"F0.imprint","IMPRINT",EDGE,{"disambiguationData":[TD([[subQ2,1.0]])],"derivedFrom":subQ1}),-1.0]])]});}
            var Q43;
            {var subQ0=sQuery(id+"F0.wireOp",EDGE,"E4.11.1");var subQ1=sQuery(id+"F0.wireOp",EDGE,"E0");var subQ2=makeQuery(id+"F0.imprint","INTERSECT",VERTEX,{"derivedFrom":[subQ1,subQ0]});Q43=makeQuery(id+"F0.imprint","IMPRINT",FACE,{"disambiguationData":[TD([[makeQuery(id+"F0.imprint","IMPRINT",EDGE,{"disambiguationData":[TD([[subQ2,1.0]])],"derivedFrom":subQ1}),-1.0]])]});}
            var Q44;
            {var subQ0=sQuery(id+"F0.wireOp",EDGE,"E4.10.2");var subQ1=sQuery(id+"F0.wireOp",EDGE,"E0");var subQ2=makeQuery(id+"F0.imprint","INTERSECT",VERTEX,{"derivedFrom":[subQ1,subQ0]});Q44=makeQuery(id+"F0.imprint","IMPRINT",FACE,{"disambiguationData":[TD([[makeQuery(id+"F0.imprint","IMPRINT",EDGE,{"disambiguationData":[TD([[subQ2,-1.0]])],"derivedFrom":subQ1}),-1.0]])]});}
            var Q45;
            {var subQ0=sQuery(id+"F0.wireOp",EDGE,"E4.1.2");var subQ1=sQuery(id+"F0.wireOp",EDGE,"E0");var subQ2=makeQuery(id+"F0.imprint","INTERSECT",VERTEX,{"derivedFrom":[subQ1,subQ0]});Q45=makeQuery(id+"F0.imprint","IMPRINT",FACE,{"disambiguationData":[TD([[makeQuery(id+"F0.imprint","IMPRINT",EDGE,{"disambiguationData":[TD([[subQ2,-1.0]])],"derivedFrom":subQ1}),-1.0]])]});}
            var Q46;
            {var subQ0=sQuery(id+"F0.wireOp",EDGE,"E4.12.2");var subQ1=sQuery(id+"F0.wireOp",EDGE,"E0");var subQ2=makeQuery(id+"F0.imprint","INTERSECT",VERTEX,{"derivedFrom":[subQ1,subQ0]});Q46=makeQuery(id+"F0.imprint","IMPRINT",FACE,{"disambiguationData":[TD([[makeQuery(id+"F0.imprint","IMPRINT",EDGE,{"disambiguationData":[TD([[subQ2,-1.0]])],"derivedFrom":subQ1}),-1.0]])]});}
            var Q47;
            {var subQ0=sQuery(id+"F0.wireOp",EDGE,"E1");var subQ1=sQuery(id+"F0.wireOp",EDGE,"E0");var subQ2=makeQuery(id+"F0.imprint","INTERSECT",VERTEX,{"derivedFrom":[subQ1,subQ0]});Q47=makeQuery(id+"F0.imprint","IMPRINT",FACE,{"disambiguationData":[TD([[makeQuery(id+"F0.imprint","IMPRINT",EDGE,{"disambiguationData":[TD([[subQ2,1.0]])],"derivedFrom":subQ1}),-1.0]])]});}
            var Q48;
            {var subQ0=sQuery(id+"F0.wireOp",EDGE,"E4.8.2");var subQ1=sQuery(id+"F0.wireOp",EDGE,"E0");var subQ2=makeQuery(id+"F0.imprint","INTERSECT",VERTEX,{"derivedFrom":[subQ1,subQ0]});Q48=makeQuery(id+"F0.imprint","IMPRINT",FACE,{"disambiguationData":[TD([[makeQuery(id+"F0.imprint","IMPRINT",EDGE,{"disambiguationData":[TD([[subQ2,1.0]])],"derivedFrom":subQ1}),-1.0]])]});}
            var Q49;
            {var subQ0=sQuery(id+"F0.wireOp",EDGE,"E6.trimOffspring");var subQ1=sQuery(id+"F0.wireOp",EDGE,"E2");var subQ2=makeQuery(id+"F0.imprint","INTERSECT",VERTEX,{"derivedFrom":[subQ1,subQ0]});Q49=makeQuery(id+"F0.imprint","IMPRINT",FACE,{"disambiguationData":[TD([[makeQuery(id+"F0.imprint","IMPRINT",EDGE,{"disambiguationData":[TD([[subQ2,1.0]])],"derivedFrom":subQ1}),1.0]])]});}
            var Q50;
            {var subQ0=sQuery(id+"F0.wireOp",EDGE,"E17.trimOffspring");var subQ1=sQuery(id+"F0.wireOp",EDGE,"E4.1.0");var subQ2=makeQuery(id+"F0.imprint","INTERSECT",VERTEX,{"derivedFrom":[subQ1,subQ0]});Q50=makeQuery(id+"F0.imprint","IMPRINT",FACE,{"disambiguationData":[TD([[makeQuery(id+"F0.imprint","IMPRINT",EDGE,{"disambiguationData":[TD([[subQ2,-1.0]])],"derivedFrom":subQ1}),1.0]])]});}
            var Q51;
            {var subQ0=sQuery(id+"F0.wireOp",EDGE,"E4.13.0");var subQ1=sQuery(id+"F0.wireOp",EDGE,"E4.12.2");var subQ2=makeQuery(id+"F0.imprint","INTERSECT",VERTEX,{"derivedFrom":[subQ1,subQ0]});Q51=makeQuery(id+"F0.imprint","IMPRINT",FACE,{"disambiguationData":[TD([[makeQuery(id+"F0.imprint","IMPRINT",EDGE,{"disambiguationData":[TD([[subQ2,-1.0]])],"derivedFrom":subQ1}),-1.0]])]});}
            var Q52;
            {var subQ0=sQuery(id+"F0.wireOp",EDGE,"E4.1.2");var subQ1=sQuery(id+"F0.wireOp",EDGE,"E0");var subQ2=makeQuery(id+"F0.imprint","INTERSECT",VERTEX,{"derivedFrom":[subQ1,subQ0]});Q52=makeQuery(id+"F0.imprint","IMPRINT",FACE,{"disambiguationData":[TD([[makeQuery(id+"F0.imprint","IMPRINT",EDGE,{"disambiguationData":[TD([[subQ2,1.0]])],"derivedFrom":subQ1}),-1.0]])]});}
            var Q53;
            {var subQ0=sQuery(id+"F0.wireOp",EDGE,"E4.1.0");var subQ1=sQuery(id+"F0.wireOp",EDGE,"E1");var subQ2=makeQuery(id+"F0.imprint","INTERSECT",VERTEX,{"derivedFrom":[subQ1,subQ0]});Q53=makeQuery(id+"F0.imprint","IMPRINT",FACE,{"disambiguationData":[TD([[makeQuery(id+"F0.imprint","IMPRINT",EDGE,{"disambiguationData":[TD([[subQ2,-1.0]])],"derivedFrom":subQ1}),-1.0]])]});}
            var Q54;
            {var subQ0=sQuery(id+"F0.wireOp",EDGE,"E4.8.0");var subQ1=sQuery(id+"F0.wireOp",EDGE,"E4.7.2");var subQ2=makeQuery(id+"F0.imprint","INTERSECT",VERTEX,{"derivedFrom":[subQ1,subQ0]});Q54=makeQuery(id+"F0.imprint","IMPRINT",FACE,{"disambiguationData":[TD([[makeQuery(id+"F0.imprint","IMPRINT",EDGE,{"disambiguationData":[TD([[subQ2,-1.0]])],"derivedFrom":subQ1}),-1.0]])]});}
            var Q55;
            {var subQ0=sQuery(id+"F0.wireOp",EDGE,"E4.3.2");var subQ1=sQuery(id+"F0.wireOp",EDGE,"E4.3.0");var subQ2=makeQuery(id+"F0.imprint","INTERSECT",VERTEX,{"derivedFrom":[subQ1,subQ0]});Q55=makeQuery(id+"F0.imprint","IMPRINT",FACE,{"disambiguationData":[TD([[makeQuery(id+"F0.imprint","IMPRINT",EDGE,{"disambiguationData":[TD([[subQ2,-1.0]])],"derivedFrom":subQ1}),1.0]])]});}
            var Q56;
            {var subQ0=sQuery(id+"F0.wireOp",EDGE,"E4.9.0");var subQ1=sQuery(id+"F0.wireOp",EDGE,"E4.8.2");var subQ2=makeQuery(id+"F0.imprint","INTERSECT",VERTEX,{"derivedFrom":[subQ1,subQ0]});Q56=makeQuery(id+"F0.imprint","IMPRINT",FACE,{"disambiguationData":[TD([[makeQuery(id+"F0.imprint","IMPRINT",EDGE,{"disambiguationData":[TD([[subQ2,-1.0]])],"derivedFrom":subQ1}),-1.0]])]});}
            var Q57;
            {var subQ0=sQuery(id+"F0.wireOp",EDGE,"E2");var subQ1=sQuery(id+"F0.wireOp",EDGE,"E0");var subQ2=makeQuery(id+"F0.imprint","INTERSECT",VERTEX,{"derivedFrom":[subQ1,subQ0]});Q57=makeQuery(id+"F0.imprint","IMPRINT",FACE,{"disambiguationData":[TD([[makeQuery(id+"F0.imprint","IMPRINT",EDGE,{"disambiguationData":[TD([[subQ2,-1.0]])],"derivedFrom":subQ1}),-1.0]])]});}
            var Q58;
            {var subQ0=sQuery(id+"F0.wireOp",EDGE,"E4.7.2");var subQ1=sQuery(id+"F0.wireOp",EDGE,"E0");var subQ2=makeQuery(id+"F0.imprint","INTERSECT",VERTEX,{"derivedFrom":[subQ1,subQ0]});Q58=makeQuery(id+"F0.imprint","IMPRINT",FACE,{"disambiguationData":[TD([[makeQuery(id+"F0.imprint","IMPRINT",EDGE,{"disambiguationData":[TD([[subQ2,1.0]])],"derivedFrom":subQ1}),-1.0]])]});}
            var Q59;
            {var subQ0=sQuery(id+"F0.wireOp",EDGE,"E4.9.2");var subQ1=sQuery(id+"F0.wireOp",EDGE,"E4.9.0");var subQ2=makeQuery(id+"F0.imprint","INTERSECT",VERTEX,{"derivedFrom":[subQ1,subQ0]});Q59=makeQuery(id+"F0.imprint","IMPRINT",FACE,{"disambiguationData":[TD([[makeQuery(id+"F0.imprint","IMPRINT",EDGE,{"disambiguationData":[TD([[subQ2,-1.0]])],"derivedFrom":subQ1}),1.0]])]});}
            var Q60;
            {var subQ0=sQuery(id+"F0.wireOp",EDGE,"E8.trimOffspring");var subQ1=sQuery(id+"F0.wireOp",EDGE,"E4.12.2");var subQ2=makeQuery(id+"F0.imprint","INTERSECT",VERTEX,{"derivedFrom":[subQ1,subQ0]});Q60=makeQuery(id+"F0.imprint","IMPRINT",FACE,{"disambiguationData":[TD([[makeQuery(id+"F0.imprint","IMPRINT",EDGE,{"disambiguationData":[TD([[subQ2,1.0]])],"derivedFrom":subQ1}),1.0]])]});}
            var Q61;
            {var subQ0=sQuery(id+"F0.wireOp",EDGE,"E17.trimOffspring");var subQ1=sQuery(id+"F0.wireOp",EDGE,"E4.2.2");var subQ2=makeQuery(id+"F0.imprint","INTERSECT",VERTEX,{"derivedFrom":[subQ1,subQ0]});Q61=makeQuery(id+"F0.imprint","IMPRINT",FACE,{"disambiguationData":[TD([[makeQuery(id+"F0.imprint","IMPRINT",EDGE,{"disambiguationData":[TD([[subQ2,-1.0]])],"derivedFrom":subQ1}),-1.0]])]});}
            var Q62;
            {var subQ0=sQuery(id+"F0.wireOp",EDGE,"E4.6.0");var subQ1=sQuery(id+"F0.wireOp",EDGE,"E4.5.0");var subQ2=makeQuery(id+"F0.imprint","INTERSECT",VERTEX,{"derivedFrom":[subQ1,subQ0]});Q62=makeQuery(id+"F0.imprint","IMPRINT",FACE,{"disambiguationData":[TD([[makeQuery(id+"F0.imprint","IMPRINT",EDGE,{"disambiguationData":[TD([[subQ2,-1.0]])],"derivedFrom":subQ1}),1.0]])]});}
            var Q63;
            {var subQ0=sQuery(id+"F0.wireOp",EDGE,"E4.11.2");var subQ1=sQuery(id+"F0.wireOp",EDGE,"E0");var subQ2=makeQuery(id+"F0.imprint","INTERSECT",VERTEX,{"derivedFrom":[subQ1,subQ0]});Q63=makeQuery(id+"F0.imprint","IMPRINT",FACE,{"disambiguationData":[TD([[makeQuery(id+"F0.imprint","IMPRINT",EDGE,{"disambiguationData":[TD([[subQ2,1.0]])],"derivedFrom":subQ1}),-1.0]])]});}
            var Q64;
            {var subQ0=sQuery(id+"F0.wireOp",EDGE,"E4.10.2");var subQ1=sQuery(id+"F0.wireOp",EDGE,"E0");var subQ2=makeQuery(id+"F0.imprint","INTERSECT",VERTEX,{"derivedFrom":[subQ1,subQ0]});Q64=makeQuery(id+"F0.imprint","IMPRINT",FACE,{"disambiguationData":[TD([[makeQuery(id+"F0.imprint","IMPRINT",EDGE,{"disambiguationData":[TD([[subQ2,1.0]])],"derivedFrom":subQ1}),-1.0]])]});}
            var Q65;
            {var subQ0=sQuery(id+"F0.wireOp",EDGE,"E4.5.0");var subQ1=sQuery(id+"F0.wireOp",EDGE,"E4.4.2");var subQ2=makeQuery(id+"F0.imprint","INTERSECT",VERTEX,{"derivedFrom":[subQ1,subQ0]});Q65=makeQuery(id+"F0.imprint","IMPRINT",FACE,{"disambiguationData":[TD([[makeQuery(id+"F0.imprint","IMPRINT",EDGE,{"disambiguationData":[TD([[subQ2,-1.0]])],"derivedFrom":subQ1}),-1.0]])]});}
            var Q66;
            {var subQ0=sQuery(id+"F0.wireOp",EDGE,"E4.10.2");var subQ1=sQuery(id+"F0.wireOp",EDGE,"E4.10.0");var subQ2=makeQuery(id+"F0.imprint","INTERSECT",VERTEX,{"derivedFrom":[subQ1,subQ0]});Q66=makeQuery(id+"F0.imprint","IMPRINT",FACE,{"disambiguationData":[TD([[makeQuery(id+"F0.imprint","IMPRINT",EDGE,{"disambiguationData":[TD([[subQ2,-1.0]])],"derivedFrom":subQ1}),1.0]])]});}
            var Q67;
            {var subQ0=sQuery(id+"F0.wireOp",EDGE,"E4.13.1");var subQ1=sQuery(id+"F0.wireOp",EDGE,"E0");var subQ2=makeQuery(id+"F0.imprint","INTERSECT",VERTEX,{"derivedFrom":[subQ1,subQ0]});Q67=makeQuery(id+"F0.imprint","IMPRINT",FACE,{"disambiguationData":[TD([[makeQuery(id+"F0.imprint","IMPRINT",EDGE,{"disambiguationData":[TD([[subQ2,1.0]])],"derivedFrom":subQ1}),-1.0]])]});}
            var Q68;
            {var subQ0=sQuery(id+"F0.wireOp",EDGE,"E4.4.2");var subQ1=sQuery(id+"F0.wireOp",EDGE,"E0");var subQ2=makeQuery(id+"F0.imprint","INTERSECT",VERTEX,{"derivedFrom":[subQ1,subQ0]});Q68=makeQuery(id+"F0.imprint","IMPRINT",FACE,{"disambiguationData":[TD([[makeQuery(id+"F0.imprint","IMPRINT",EDGE,{"disambiguationData":[TD([[subQ2,1.0]])],"derivedFrom":subQ1}),-1.0]])]});}
            var Q69;
            {var subQ0=sQuery(id+"F0.wireOp",EDGE,"E4.4.0");var subQ1=sQuery(id+"F0.wireOp",EDGE,"E4.3.2");var subQ2=makeQuery(id+"F0.imprint","INTERSECT",VERTEX,{"derivedFrom":[subQ1,subQ0]});Q69=makeQuery(id+"F0.imprint","IMPRINT",FACE,{"disambiguationData":[TD([[makeQuery(id+"F0.imprint","IMPRINT",EDGE,{"disambiguationData":[TD([[subQ2,-1.0]])],"derivedFrom":subQ1}),-1.0]])]});}
            var Q70;
            {var subQ0=sQuery(id+"F0.wireOp",EDGE,"E4.12.0");var subQ1=sQuery(id+"F0.wireOp",EDGE,"E4.11.2");var subQ2=makeQuery(id+"F0.imprint","INTERSECT",VERTEX,{"derivedFrom":[subQ1,subQ0]});Q70=makeQuery(id+"F0.imprint","IMPRINT",FACE,{"disambiguationData":[TD([[makeQuery(id+"F0.imprint","IMPRINT",EDGE,{"disambiguationData":[TD([[subQ2,-1.0]])],"derivedFrom":subQ1}),-1.0]])]});}
            var Q71;
            {var subQ0=sQuery(id+"F0.wireOp",EDGE,"E4.2.2");var subQ1=sQuery(id+"F0.wireOp",EDGE,"E0");var subQ2=makeQuery(id+"F0.imprint","INTERSECT",VERTEX,{"derivedFrom":[subQ1,subQ0]});Q71=makeQuery(id+"F0.imprint","IMPRINT",FACE,{"disambiguationData":[TD([[makeQuery(id+"F0.imprint","IMPRINT",EDGE,{"disambiguationData":[TD([[subQ2,1.0]])],"derivedFrom":subQ1}),-1.0]])]});}
            var Q72;
            {var subQ0=sQuery(id+"F0.wireOp",EDGE,"E3");var subQ1=sQuery(id+"F0.wireOp",EDGE,"E0");var subQ2=makeQuery(id+"F0.imprint","INTERSECT",VERTEX,{"disambiguationData":[OD(0.0)],"derivedFrom":[subQ1,subQ0]});Q72=makeQuery(id+"F0.imprint","IMPRINT",FACE,{"disambiguationData":[TD([[makeQuery(id+"F0.imprint","IMPRINT",EDGE,{"disambiguationData":[TD([[subQ2,-1.0]])],"derivedFrom":subQ1}),1.0]])]});}
            var Q73;
            {var subQ0=sQuery(id+"F0.wireOp",EDGE,"E17.trimOffspring");var subQ1=sQuery(id+"F0.wireOp",EDGE,"E0");var subQ2=makeQuery(id+"F0.imprint","INTERSECT",VERTEX,{"disambiguationData":[OD(0.0)],"derivedFrom":[subQ1,subQ0]});Q73=makeQuery(id+"F0.imprint","IMPRINT",FACE,{"disambiguationData":[TD([[makeQuery(id+"F0.imprint","IMPRINT",EDGE,{"disambiguationData":[TD([[subQ2,-1.0]])],"derivedFrom":subQ1}),1.0]])]});}
            var Q74;
            {var subQ0=sQuery(id+"F0.wireOp",EDGE,"E4.4.0");var subQ1=sQuery(id+"F0.wireOp",EDGE,"E0");var subQ2=makeQuery(id+"F0.imprint","INTERSECT",VERTEX,{"disambiguationData":[OD(0.0)],"derivedFrom":[subQ1,subQ0]});Q74=makeQuery(id+"F0.imprint","IMPRINT",FACE,{"disambiguationData":[TD([[makeQuery(id+"F0.imprint","IMPRINT",EDGE,{"disambiguationData":[TD([[subQ2,-1.0]])],"derivedFrom":subQ1}),1.0]])]});}
            var Q75;
            {var subQ0=sQuery(id+"F0.wireOp",EDGE,"E4.5.0");var subQ1=sQuery(id+"F0.wireOp",EDGE,"E0");var subQ2=makeQuery(id+"F0.imprint","INTERSECT",VERTEX,{"disambiguationData":[OD(0.0)],"derivedFrom":[subQ1,subQ0]});Q75=makeQuery(id+"F0.imprint","IMPRINT",FACE,{"disambiguationData":[TD([[makeQuery(id+"F0.imprint","IMPRINT",EDGE,{"disambiguationData":[TD([[subQ2,-1.0]])],"derivedFrom":subQ1}),1.0]])]});}
            var Q76;
            {var subQ0=sQuery(id+"F0.wireOp",EDGE,"E4.6.0");var subQ1=sQuery(id+"F0.wireOp",EDGE,"E0");var subQ2=makeQuery(id+"F0.imprint","INTERSECT",VERTEX,{"disambiguationData":[OD(0.0)],"derivedFrom":[subQ1,subQ0]});Q76=makeQuery(id+"F0.imprint","IMPRINT",FACE,{"disambiguationData":[TD([[makeQuery(id+"F0.imprint","IMPRINT",EDGE,{"disambiguationData":[TD([[subQ2,-1.0]])],"derivedFrom":subQ1}),1.0]])]});}
            var Q77;
            {var subQ0=sQuery(id+"F0.wireOp",EDGE,"E4.6.0");var subQ1=sQuery(id+"F0.wireOp",EDGE,"E4.5.2");var subQ2=makeQuery(id+"F0.imprint","INTERSECT",VERTEX,{"derivedFrom":[subQ1,subQ0]});Q77=makeQuery(id+"F0.imprint","IMPRINT",FACE,{"disambiguationData":[TD([[makeQuery(id+"F0.imprint","IMPRINT",EDGE,{"disambiguationData":[TD([[subQ2,-1.0]])],"derivedFrom":subQ1}),-1.0]])]});}
            var Q78;
            {var subQ0=sQuery(id+"F0.wireOp",EDGE,"E4.5.2");var subQ1=sQuery(id+"F0.wireOp",EDGE,"E0");var subQ2=makeQuery(id+"F0.imprint","INTERSECT",VERTEX,{"derivedFrom":[subQ1,subQ0]});Q78=makeQuery(id+"F0.imprint","IMPRINT",FACE,{"disambiguationData":[TD([[makeQuery(id+"F0.imprint","IMPRINT",EDGE,{"disambiguationData":[TD([[subQ2,-1.0]])],"derivedFrom":subQ1}),-1.0]])]});}
            var Q79;
            {var subQ0=sQuery(id+"F0.wireOp",EDGE,"E4.11.0");var subQ1=sQuery(id+"F0.wireOp",EDGE,"E4.10.2");var subQ2=makeQuery(id+"F0.imprint","INTERSECT",VERTEX,{"derivedFrom":[subQ1,subQ0]});Q79=makeQuery(id+"F0.imprint","IMPRINT",FACE,{"disambiguationData":[TD([[makeQuery(id+"F0.imprint","IMPRINT",EDGE,{"disambiguationData":[TD([[subQ2,-1.0]])],"derivedFrom":subQ1}),-1.0]])]});}
            var Q80;
            {var subQ0=sQuery(id+"F0.wireOp",EDGE,"E4.3.0");var subQ1=sQuery(id+"F0.wireOp",EDGE,"E4.2.2");var subQ2=makeQuery(id+"F0.imprint","INTERSECT",VERTEX,{"derivedFrom":[subQ1,subQ0]});Q80=makeQuery(id+"F0.imprint","IMPRINT",FACE,{"disambiguationData":[TD([[makeQuery(id+"F0.imprint","IMPRINT",EDGE,{"disambiguationData":[TD([[subQ2,-1.0]])],"derivedFrom":subQ1}),-1.0]])]});}
            var Q81;
            {var subQ0=sQuery(id+"F0.wireOp",EDGE,"E3");var subQ1=sQuery(id+"F0.wireOp",EDGE,"E2");var subQ2=makeQuery(id+"F0.imprint","INTERSECT",VERTEX,{"derivedFrom":[subQ1,subQ0]});Q81=makeQuery(id+"F0.imprint","IMPRINT",FACE,{"disambiguationData":[TD([[makeQuery(id+"F0.imprint","IMPRINT",EDGE,{"disambiguationData":[TD([[subQ2,1.0]])],"derivedFrom":subQ1}),1.0]])]});}
            var Q82;
            {var subQ0=sQuery(id+"F0.wireOp",EDGE,"E4.12.2");var subQ1=sQuery(id+"F0.wireOp",EDGE,"E0");var subQ2=makeQuery(id+"F0.imprint","INTERSECT",VERTEX,{"derivedFrom":[subQ1,subQ0]});Q82=makeQuery(id+"F0.imprint","IMPRINT",FACE,{"disambiguationData":[TD([[makeQuery(id+"F0.imprint","IMPRINT",EDGE,{"disambiguationData":[TD([[subQ2,1.0]])],"derivedFrom":subQ1}),-1.0]])]});}
            var Q83;
            {var subQ0=sQuery(id+"F0.wireOp",EDGE,"E4.3.2");var subQ1=sQuery(id+"F0.wireOp",EDGE,"E0");var subQ2=makeQuery(id+"F0.imprint","INTERSECT",VERTEX,{"derivedFrom":[subQ1,subQ0]});Q83=makeQuery(id+"F0.imprint","IMPRINT",FACE,{"disambiguationData":[TD([[makeQuery(id+"F0.imprint","IMPRINT",EDGE,{"disambiguationData":[TD([[subQ2,1.0]])],"derivedFrom":subQ1}),-1.0]])]});}
            var Q84;
            {var subQ0=sQuery(id+"F0.wireOp",EDGE,"E4.4.1");var subQ1=sQuery(id+"F0.wireOp",EDGE,"E0");var subQ2=makeQuery(id+"F0.imprint","INTERSECT",VERTEX,{"derivedFrom":[subQ1,subQ0]});Q84=makeQuery(id+"F0.imprint","IMPRINT",FACE,{"disambiguationData":[TD([[makeQuery(id+"F0.imprint","IMPRINT",EDGE,{"disambiguationData":[TD([[subQ2,1.0]])],"derivedFrom":subQ1}),-1.0]])]});}
            var Q85;
            {var subQ0=sQuery(id+"F0.wireOp",EDGE,"E4.1.1");var subQ1=sQuery(id+"F0.wireOp",EDGE,"E0");var subQ2=makeQuery(id+"F0.imprint","INTERSECT",VERTEX,{"derivedFrom":[subQ1,subQ0]});Q85=makeQuery(id+"F0.imprint","IMPRINT",FACE,{"disambiguationData":[TD([[makeQuery(id+"F0.imprint","IMPRINT",EDGE,{"disambiguationData":[TD([[subQ2,1.0]])],"derivedFrom":subQ1}),-1.0]])]});}
            var Q86;
            {var subQ0=sQuery(id+"F0.wireOp",EDGE,"E4.7.0");var subQ1=sQuery(id+"F0.wireOp",EDGE,"E4.6.2");var subQ2=makeQuery(id+"F0.imprint","INTERSECT",VERTEX,{"derivedFrom":[subQ1,subQ0]});Q86=makeQuery(id+"F0.imprint","IMPRINT",FACE,{"disambiguationData":[TD([[makeQuery(id+"F0.imprint","IMPRINT",EDGE,{"disambiguationData":[TD([[subQ2,-1.0]])],"derivedFrom":subQ1}),-1.0]])]});}
            var Q87;
            {var subQ0=sQuery(id+"F0.wireOp",EDGE,"E4.10.0");var subQ1=sQuery(id+"F0.wireOp",EDGE,"E4.9.2");var subQ2=makeQuery(id+"F0.imprint","INTERSECT",VERTEX,{"derivedFrom":[subQ1,subQ0]});Q87=makeQuery(id+"F0.imprint","IMPRINT",FACE,{"disambiguationData":[TD([[makeQuery(id+"F0.imprint","IMPRINT",EDGE,{"disambiguationData":[TD([[subQ2,-1.0]])],"derivedFrom":subQ1}),-1.0]])]});}
            var Q88;
            {var subQ0=sQuery(id+"F0.wireOp",EDGE,"E4.6.2");var subQ1=sQuery(id+"F0.wireOp",EDGE,"E0");var subQ2=makeQuery(id+"F0.imprint","INTERSECT",VERTEX,{"derivedFrom":[subQ1,subQ0]});Q88=makeQuery(id+"F0.imprint","IMPRINT",FACE,{"disambiguationData":[TD([[makeQuery(id+"F0.imprint","IMPRINT",EDGE,{"disambiguationData":[TD([[subQ2,-1.0]])],"derivedFrom":subQ1}),-1.0]])]});}
            var Q89;
            {var subQ0=sQuery(id+"F0.wireOp",EDGE,"E17.trimOffspring");var subQ1=sQuery(id+"F0.wireOp",EDGE,"E4.1.2");var subQ2=makeQuery(id+"F0.imprint","INTERSECT",VERTEX,{"derivedFrom":[subQ1,subQ0]});Q89=makeQuery(id+"F0.imprint","IMPRINT",FACE,{"disambiguationData":[TD([[makeQuery(id+"F0.imprint","IMPRINT",EDGE,{"disambiguationData":[TD([[subQ2,-1.0]])],"derivedFrom":subQ1}),-1.0]])]});}
            var Q90;
            {var subQ0=sQuery(id+"F0.wireOp",EDGE,"E5.trimOffspring");var subQ1=sQuery(id+"F0.wireOp",EDGE,"E4.1.2");var subQ2=makeQuery(id+"F0.imprint","INTERSECT",VERTEX,{"derivedFrom":[subQ1,subQ0]});Q90=makeQuery(id+"F0.imprint","IMPRINT",FACE,{"disambiguationData":[TD([[makeQuery(id+"F0.imprint","IMPRINT",EDGE,{"disambiguationData":[TD([[subQ2,1.0]])],"derivedFrom":subQ1}),1.0]])]});}
            var Q91;
            {var subQ0=sQuery(id+"F0.wireOp",EDGE,"E4.5.2");var subQ1=sQuery(id+"F0.wireOp",EDGE,"E0");var subQ2=makeQuery(id+"F0.imprint","INTERSECT",VERTEX,{"derivedFrom":[subQ1,subQ0]});Q91=makeQuery(id+"F0.imprint","IMPRINT",FACE,{"disambiguationData":[TD([[makeQuery(id+"F0.imprint","IMPRINT",EDGE,{"disambiguationData":[TD([[subQ2,1.0]])],"derivedFrom":subQ1}),-1.0]])]});}
            var Q92;
            {var subQ0=sQuery(id+"F0.wireOp",EDGE,"E4.10.0");var subQ1=sQuery(id+"F0.wireOp",EDGE,"E4.9.0");var subQ2=makeQuery(id+"F0.imprint","INTERSECT",VERTEX,{"derivedFrom":[subQ1,subQ0]});Q92=makeQuery(id+"F0.imprint","IMPRINT",FACE,{"disambiguationData":[TD([[makeQuery(id+"F0.imprint","IMPRINT",EDGE,{"disambiguationData":[TD([[subQ2,-1.0]])],"derivedFrom":subQ1}),1.0]])]});}
            var Q93;
            {var subQ0=sQuery(id+"F0.wireOp",EDGE,"E4.13.0");var subQ1=sQuery(id+"F0.wireOp",EDGE,"E3");var subQ2=makeQuery(id+"F0.imprint","INTERSECT",VERTEX,{"derivedFrom":[subQ1,subQ0]});Q93=makeQuery(id+"F0.imprint","IMPRINT",FACE,{"disambiguationData":[TD([[makeQuery(id+"F0.imprint","IMPRINT",EDGE,{"disambiguationData":[TD([[subQ2,-1.0]])],"derivedFrom":subQ1}),-1.0]])]});}
            var Q94;
            {var subQ0=sQuery(id+"F0.wireOp",EDGE,"E4.11.2");var subQ1=sQuery(id+"F0.wireOp",EDGE,"E4.11.0");var subQ2=makeQuery(id+"F0.imprint","INTERSECT",VERTEX,{"derivedFrom":[subQ1,subQ0]});Q94=makeQuery(id+"F0.imprint","IMPRINT",FACE,{"disambiguationData":[TD([[makeQuery(id+"F0.imprint","IMPRINT",EDGE,{"disambiguationData":[TD([[subQ2,-1.0]])],"derivedFrom":subQ1}),1.0]])]});}
            var Q95;
            {var subQ0=sQuery(id+"F0.wireOp",EDGE,"E4.12.2");var subQ1=sQuery(id+"F0.wireOp",EDGE,"E4.12.0");var subQ2=makeQuery(id+"F0.imprint","INTERSECT",VERTEX,{"derivedFrom":[subQ1,subQ0]});Q95=makeQuery(id+"F0.imprint","IMPRINT",FACE,{"disambiguationData":[TD([[makeQuery(id+"F0.imprint","IMPRINT",EDGE,{"disambiguationData":[TD([[subQ2,-1.0]])],"derivedFrom":subQ1}),1.0]])]});}
            var Q96;
            {var subQ0=sQuery(id+"F0.wireOp",EDGE,"E4.5.0");var subQ1=sQuery(id+"F0.wireOp",EDGE,"E4.4.0");var subQ2=makeQuery(id+"F0.imprint","INTERSECT",VERTEX,{"derivedFrom":[subQ1,subQ0]});Q96=makeQuery(id+"F0.imprint","IMPRINT",FACE,{"disambiguationData":[TD([[makeQuery(id+"F0.imprint","IMPRINT",EDGE,{"disambiguationData":[TD([[subQ2,-1.0]])],"derivedFrom":subQ1}),1.0]])]});}
            var Q97;
            {var subQ0=sQuery(id+"F0.wireOp",EDGE,"E4.8.0");var subQ1=sQuery(id+"F0.wireOp",EDGE,"E4.7.0");var subQ2=makeQuery(id+"F0.imprint","INTERSECT",VERTEX,{"derivedFrom":[subQ1,subQ0]});Q97=makeQuery(id+"F0.imprint","IMPRINT",FACE,{"disambiguationData":[TD([[makeQuery(id+"F0.imprint","IMPRINT",EDGE,{"disambiguationData":[TD([[subQ2,-1.0]])],"derivedFrom":subQ1}),1.0]])]});}
            var Q98;
            {var subQ0=sQuery(id+"F0.wireOp",EDGE,"E4.11.0");var subQ1=sQuery(id+"F0.wireOp",EDGE,"E4.10.0");var subQ2=makeQuery(id+"F0.imprint","INTERSECT",VERTEX,{"derivedFrom":[subQ1,subQ0]});Q98=makeQuery(id+"F0.imprint","IMPRINT",FACE,{"disambiguationData":[TD([[makeQuery(id+"F0.imprint","IMPRINT",EDGE,{"disambiguationData":[TD([[subQ2,-1.0]])],"derivedFrom":subQ1}),1.0]])]});}
            var Q99;
            {var subQ0=sQuery(id+"F0.wireOp",EDGE,"E17.trimOffspring");var subQ1=sQuery(id+"F0.wireOp",EDGE,"E4.2.2");var subQ2=makeQuery(id+"F0.imprint","INTERSECT",VERTEX,{"derivedFrom":[subQ1,subQ0]});Q99=makeQuery(id+"F0.imprint","IMPRINT",FACE,{"disambiguationData":[TD([[makeQuery(id+"F0.imprint","IMPRINT",EDGE,{"disambiguationData":[TD([[subQ2,-1.0]])],"derivedFrom":subQ1}),1.0]])]});}
            var Q100;
            {var subQ0=sQuery(id+"F0.wireOp",EDGE,"E3");var subQ1=sQuery(id+"F0.wireOp",EDGE,"E1");var subQ2=makeQuery(id+"F0.imprint","INTERSECT",VERTEX,{"derivedFrom":[subQ1,subQ0]});Q100=makeQuery(id+"F0.imprint","IMPRINT",FACE,{"disambiguationData":[TD([[makeQuery(id+"F0.imprint","IMPRINT",EDGE,{"disambiguationData":[TD([[subQ2,-1.0]])],"derivedFrom":subQ1}),-1.0]])]});}
            var Q101;
            {var subQ0=sQuery(id+"F0.wireOp",EDGE,"E4.6.2");var subQ1=sQuery(id+"F0.wireOp",EDGE,"E0");var subQ2=makeQuery(id+"F0.imprint","INTERSECT",VERTEX,{"derivedFrom":[subQ1,subQ0]});Q101=makeQuery(id+"F0.imprint","IMPRINT",FACE,{"disambiguationData":[TD([[makeQuery(id+"F0.imprint","IMPRINT",EDGE,{"disambiguationData":[TD([[subQ2,1.0]])],"derivedFrom":subQ1}),-1.0]])]});}
            var Q102;
            {var subQ0=sQuery(id+"F0.wireOp",EDGE,"E4.4.0");var subQ1=sQuery(id+"F0.wireOp",EDGE,"E4.3.0");var subQ2=makeQuery(id+"F0.imprint","INTERSECT",VERTEX,{"derivedFrom":[subQ1,subQ0]});Q102=makeQuery(id+"F0.imprint","IMPRINT",FACE,{"disambiguationData":[TD([[makeQuery(id+"F0.imprint","IMPRINT",EDGE,{"disambiguationData":[TD([[subQ2,-1.0]])],"derivedFrom":subQ1}),1.0]])]});}
            var Q103;
            {var subQ0=sQuery(id+"F0.wireOp",EDGE,"E4.1.2");var subQ1=sQuery(id+"F0.wireOp",EDGE,"E4.1.0");var subQ2=makeQuery(id+"F0.imprint","INTERSECT",VERTEX,{"derivedFrom":[subQ1,subQ0]});Q103=makeQuery(id+"F0.imprint","IMPRINT",FACE,{"disambiguationData":[TD([[makeQuery(id+"F0.imprint","IMPRINT",EDGE,{"disambiguationData":[TD([[subQ2,-1.0]])],"derivedFrom":subQ1}),1.0]])]});}
            var Q104;
            {var subQ0=sQuery(id+"F0.wireOp",EDGE,"E4.8.2");var subQ1=sQuery(id+"F0.wireOp",EDGE,"E4.8.0");var subQ2=makeQuery(id+"F0.imprint","INTERSECT",VERTEX,{"derivedFrom":[subQ1,subQ0]});Q104=makeQuery(id+"F0.imprint","IMPRINT",FACE,{"disambiguationData":[TD([[makeQuery(id+"F0.imprint","IMPRINT",EDGE,{"disambiguationData":[TD([[subQ2,-1.0]])],"derivedFrom":subQ1}),1.0]])]});}
            var Q105;
            {var subQ0=sQuery(id+"F0.wireOp",EDGE,"E12.trimOffspring");var subQ1=sQuery(id+"F0.wireOp",EDGE,"E4.8.2");var subQ2=makeQuery(id+"F0.imprint","INTERSECT",VERTEX,{"derivedFrom":[subQ1,subQ0]});Q105=makeQuery(id+"F0.imprint","IMPRINT",FACE,{"disambiguationData":[TD([[makeQuery(id+"F0.imprint","IMPRINT",EDGE,{"disambiguationData":[TD([[subQ2,1.0]])],"derivedFrom":subQ1}),1.0]])]});}
            var Q106;
            {var subQ0=sQuery(id+"F0.wireOp",EDGE,"E4.4.2");var subQ1=sQuery(id+"F0.wireOp",EDGE,"E4.4.0");var subQ2=makeQuery(id+"F0.imprint","INTERSECT",VERTEX,{"derivedFrom":[subQ1,subQ0]});Q106=makeQuery(id+"F0.imprint","IMPRINT",FACE,{"disambiguationData":[TD([[makeQuery(id+"F0.imprint","IMPRINT",EDGE,{"disambiguationData":[TD([[subQ2,-1.0]])],"derivedFrom":subQ1}),1.0]])]});}
            var Q107;
            {var subQ0=sQuery(id+"F0.wireOp",EDGE,"E4.13.0");var subQ1=sQuery(id+"F0.wireOp",EDGE,"E4.12.0");var subQ2=makeQuery(id+"F0.imprint","INTERSECT",VERTEX,{"derivedFrom":[subQ1,subQ0]});Q107=makeQuery(id+"F0.imprint","IMPRINT",FACE,{"disambiguationData":[TD([[makeQuery(id+"F0.imprint","IMPRINT",EDGE,{"disambiguationData":[TD([[subQ2,-1.0]])],"derivedFrom":subQ1}),1.0]])]});}
            var Q108;
            {var subQ0=sQuery(id+"F0.wireOp",EDGE,"E3");var subQ1=sQuery(id+"F0.wireOp",EDGE,"E1");var subQ2=makeQuery(id+"F0.imprint","INTERSECT",VERTEX,{"derivedFrom":[subQ1,subQ0]});Q108=makeQuery(id+"F0.imprint","IMPRINT",FACE,{"disambiguationData":[TD([[makeQuery(id+"F0.imprint","IMPRINT",EDGE,{"disambiguationData":[TD([[subQ2,-1.0]])],"derivedFrom":subQ1}),1.0]])]});}
            var Q109;
            {var subQ0=sQuery(id+"F0.wireOp",EDGE,"E4.5.2");var subQ1=sQuery(id+"F0.wireOp",EDGE,"E4.5.0");var subQ2=makeQuery(id+"F0.imprint","INTERSECT",VERTEX,{"derivedFrom":[subQ1,subQ0]});Q109=makeQuery(id+"F0.imprint","IMPRINT",FACE,{"disambiguationData":[TD([[makeQuery(id+"F0.imprint","IMPRINT",EDGE,{"disambiguationData":[TD([[subQ2,-1.0]])],"derivedFrom":subQ1}),1.0]])]});}
            var Q110;
            {var subQ0=sQuery(id+"F0.wireOp",EDGE,"E4.9.0");var subQ1=sQuery(id+"F0.wireOp",EDGE,"E4.8.0");var subQ2=makeQuery(id+"F0.imprint","INTERSECT",VERTEX,{"derivedFrom":[subQ1,subQ0]});Q110=makeQuery(id+"F0.imprint","IMPRINT",FACE,{"disambiguationData":[TD([[makeQuery(id+"F0.imprint","IMPRINT",EDGE,{"disambiguationData":[TD([[subQ2,-1.0]])],"derivedFrom":subQ1}),1.0]])]});}
            var Q111;
            {var subQ0=sQuery(id+"F0.wireOp",EDGE,"E13.trimOffspring");var subQ1=sQuery(id+"F0.wireOp",EDGE,"E4.7.2");var subQ2=makeQuery(id+"F0.imprint","INTERSECT",VERTEX,{"derivedFrom":[subQ1,subQ0]});Q111=makeQuery(id+"F0.imprint","IMPRINT",FACE,{"disambiguationData":[TD([[makeQuery(id+"F0.imprint","IMPRINT",EDGE,{"disambiguationData":[TD([[subQ2,1.0]])],"derivedFrom":subQ1}),1.0]])]});}
            var Q112;
            {var subQ0=sQuery(id+"F0.wireOp",EDGE,"E7.trimOffspring");var subQ1=sQuery(id+"F0.wireOp",EDGE,"E4.13.2");var subQ2=makeQuery(id+"F0.imprint","INTERSECT",VERTEX,{"derivedFrom":[subQ1,subQ0]});Q112=makeQuery(id+"F0.imprint","IMPRINT",FACE,{"disambiguationData":[TD([[makeQuery(id+"F0.imprint","IMPRINT",EDGE,{"disambiguationData":[TD([[subQ2,1.0]])],"derivedFrom":subQ1}),1.0]])]});}
            var Q113;
            {var subQ0=sQuery(id+"F0.wireOp",EDGE,"E14.trimOffspring");var subQ1=sQuery(id+"F0.wireOp",EDGE,"E4.6.2");var subQ2=makeQuery(id+"F0.imprint","INTERSECT",VERTEX,{"derivedFrom":[subQ1,subQ0]});Q113=makeQuery(id+"F0.imprint","IMPRINT",FACE,{"disambiguationData":[TD([[makeQuery(id+"F0.imprint","IMPRINT",EDGE,{"disambiguationData":[TD([[subQ2,1.0]])],"derivedFrom":subQ1}),1.0]])]});}
            var Q114;
            {var subQ0=sQuery(id+"F0.wireOp",EDGE,"E15.trimOffspring");var subQ1=sQuery(id+"F0.wireOp",EDGE,"E4.5.2");var subQ2=makeQuery(id+"F0.imprint","INTERSECT",VERTEX,{"derivedFrom":[subQ1,subQ0]});Q114=makeQuery(id+"F0.imprint","IMPRINT",FACE,{"disambiguationData":[TD([[makeQuery(id+"F0.imprint","IMPRINT",EDGE,{"disambiguationData":[TD([[subQ2,1.0]])],"derivedFrom":subQ1}),1.0]])]});}
            var Q115;
            {var subQ0=sQuery(id+"F0.wireOp",EDGE,"E18.trimOffspring");var subQ1=sQuery(id+"F0.wireOp",EDGE,"E4.2.0");var subQ2=makeQuery(id+"F0.imprint","INTERSECT",VERTEX,{"derivedFrom":[subQ1,subQ0]});Q115=makeQuery(id+"F0.imprint","IMPRINT",FACE,{"disambiguationData":[TD([[makeQuery(id+"F0.imprint","IMPRINT",EDGE,{"disambiguationData":[TD([[subQ2,1.0]])],"derivedFrom":subQ1}),1.0]])]});}
            var Q116;
            {var subQ0=sQuery(id+"F0.wireOp",EDGE,"E6.trimOffspring");var subQ1=sQuery(id+"F0.wireOp",EDGE,"E1");var subQ2=makeQuery(id+"F0.imprint","INTERSECT",VERTEX,{"derivedFrom":[subQ1,subQ0]});Q116=makeQuery(id+"F0.imprint","IMPRINT",FACE,{"disambiguationData":[TD([[makeQuery(id+"F0.imprint","IMPRINT",EDGE,{"disambiguationData":[TD([[subQ2,1.0]])],"derivedFrom":subQ1}),1.0]])]});}
            var Q117;
            {var subQ0=sQuery(id+"F0.wireOp",EDGE,"E11.trimOffspring");var subQ1=sQuery(id+"F0.wireOp",EDGE,"E4.9.2");var subQ2=makeQuery(id+"F0.imprint","INTERSECT",VERTEX,{"derivedFrom":[subQ1,subQ0]});Q117=makeQuery(id+"F0.imprint","IMPRINT",FACE,{"disambiguationData":[TD([[makeQuery(id+"F0.imprint","IMPRINT",EDGE,{"disambiguationData":[TD([[subQ2,1.0]])],"derivedFrom":subQ1}),1.0]])]});}
            var Q118;
            {var subQ0=sQuery(id+"F0.wireOp",EDGE,"E18.trimOffspring");var subQ1=sQuery(id+"F0.wireOp",EDGE,"E4.3.2");var subQ2=makeQuery(id+"F0.imprint","INTERSECT",VERTEX,{"derivedFrom":[subQ1,subQ0]});Q118=makeQuery(id+"F0.imprint","IMPRINT",FACE,{"disambiguationData":[TD([[makeQuery(id+"F0.imprint","IMPRINT",EDGE,{"disambiguationData":[TD([[subQ2,1.0]])],"derivedFrom":subQ1}),1.0]])]});}
            var Q119;
            {var subQ0=sQuery(id+"F0.wireOp",EDGE,"E4.7.0");var subQ1=sQuery(id+"F0.wireOp",EDGE,"E4.6.0");var subQ2=makeQuery(id+"F0.imprint","INTERSECT",VERTEX,{"derivedFrom":[subQ1,subQ0]});Q119=makeQuery(id+"F0.imprint","IMPRINT",FACE,{"disambiguationData":[TD([[makeQuery(id+"F0.imprint","IMPRINT",EDGE,{"disambiguationData":[TD([[subQ2,-1.0]])],"derivedFrom":subQ1}),1.0]])]});}
            var Q120;
            {var subQ0=sQuery(id+"F0.wireOp",EDGE,"E10.trimOffspring");var subQ1=sQuery(id+"F0.wireOp",EDGE,"E4.10.2");var subQ2=makeQuery(id+"F0.imprint","INTERSECT",VERTEX,{"derivedFrom":[subQ1,subQ0]});Q120=makeQuery(id+"F0.imprint","IMPRINT",FACE,{"disambiguationData":[TD([[makeQuery(id+"F0.imprint","IMPRINT",EDGE,{"disambiguationData":[TD([[subQ2,1.0]])],"derivedFrom":subQ1}),1.0]])]});}
            var Q121;
            {var subQ0=sQuery(id+"F0.wireOp",EDGE,"E4.7.2");var subQ1=sQuery(id+"F0.wireOp",EDGE,"E4.7.0");var subQ2=makeQuery(id+"F0.imprint","INTERSECT",VERTEX,{"derivedFrom":[subQ1,subQ0]});Q121=makeQuery(id+"F0.imprint","IMPRINT",FACE,{"disambiguationData":[TD([[makeQuery(id+"F0.imprint","IMPRINT",EDGE,{"disambiguationData":[TD([[subQ2,-1.0]])],"derivedFrom":subQ1}),1.0]])]});}
            var Q122;
            {var subQ0=sQuery(id+"F0.wireOp",EDGE,"E16.trimOffspring");var subQ1=sQuery(id+"F0.wireOp",EDGE,"E4.4.2");var subQ2=makeQuery(id+"F0.imprint","INTERSECT",VERTEX,{"derivedFrom":[subQ1,subQ0]});Q122=makeQuery(id+"F0.imprint","IMPRINT",FACE,{"disambiguationData":[TD([[makeQuery(id+"F0.imprint","IMPRINT",EDGE,{"disambiguationData":[TD([[subQ2,1.0]])],"derivedFrom":subQ1}),1.0]])]});}
            var Q123;
            {var subQ0=sQuery(id+"F0.wireOp",EDGE,"E4.12.0");var subQ1=sQuery(id+"F0.wireOp",EDGE,"E4.11.0");var subQ2=makeQuery(id+"F0.imprint","INTERSECT",VERTEX,{"derivedFrom":[subQ1,subQ0]});Q123=makeQuery(id+"F0.imprint","IMPRINT",FACE,{"disambiguationData":[TD([[makeQuery(id+"F0.imprint","IMPRINT",EDGE,{"disambiguationData":[TD([[subQ2,-1.0]])],"derivedFrom":subQ1}),1.0]])]});}
            var Q124;
            {var subQ0=sQuery(id+"F0.wireOp",EDGE,"E9.trimOffspring");var subQ1=sQuery(id+"F0.wireOp",EDGE,"E4.11.2");var subQ2=makeQuery(id+"F0.imprint","INTERSECT",VERTEX,{"derivedFrom":[subQ1,subQ0]});Q124=makeQuery(id+"F0.imprint","IMPRINT",FACE,{"disambiguationData":[TD([[makeQuery(id+"F0.imprint","IMPRINT",EDGE,{"disambiguationData":[TD([[subQ2,1.0]])],"derivedFrom":subQ1}),1.0]])]});}
            var Q125;
            {var subQ0=sQuery(id+"F0.wireOp",EDGE,"E4.6.2");var subQ1=sQuery(id+"F0.wireOp",EDGE,"E4.6.0");var subQ2=makeQuery(id+"F0.imprint","INTERSECT",VERTEX,{"derivedFrom":[subQ1,subQ0]});Q125=makeQuery(id+"F0.imprint","IMPRINT",FACE,{"disambiguationData":[TD([[makeQuery(id+"F0.imprint","IMPRINT",EDGE,{"disambiguationData":[TD([[subQ2,-1.0]])],"derivedFrom":subQ1}),1.0]])]});}
            extrude(context, id + "F3", {"entities" : qUnion([Q0, Q1, Q2, Q3, Q4, Q5, Q6, Q7, Q8, Q9, Q10, Q11, Q12, Q13, Q14, Q15, Q16, Q17, Q18, Q19, Q20, Q21, Q22, Q23, Q24, Q25, Q26, Q27, Q28, Q29, Q30, Q31, Q32, Q33, Q34, Q35, Q36, Q37, Q38, Q39, Q40, Q41, Q42, Q43, Q44, Q45, Q46, Q47, Q48, Q49, Q50, Q51, Q52, Q53, Q54, Q55, Q56, Q57, Q58, Q59, Q60, Q61, Q62, Q63, Q64, Q65, Q66, Q67, Q68, Q69, Q70, Q71, Q72, Q73, Q74, Q75, Q76, Q77, Q78, Q79, Q80, Q81, Q82, Q83, Q84, Q85, Q86, Q87, Q88, Q89, Q90, Q91, Q92, Q93, Q94, Q95, Q96, Q97, Q98, Q99, Q100, Q101, Q102, Q103, Q104, Q105, Q106, Q107, Q108, Q109, Q110, Q111, Q112, Q113, Q114, Q115, Q116, Q117, Q118, Q119, Q120, Q121, Q122, Q123, Q124, Q125]), "operationType" : NewBodyOperationType.ADD, "oppositeDirection" : true, "depth" : 2 * mm, "offsetDistance" : 25 * mm});
        }
        {
            var Q0;
            Q0=makeQuery(id+"F2.opExtrude","CAP_FACE",FACE,{"disambiguationData":[OSD([sQuery(id+"F0.wireOp",EDGE,"E0"),sQuery(id+"F0.wireOp",EDGE,"E3"),sQuery(id+"F0.wireOp",EDGE,"E4.1.0"),sQuery(id+"F0.wireOp",EDGE,"E4.3.0"),sQuery(id+"F0.wireOp",EDGE,"E4.4.0"),sQuery(id+"F0.wireOp",EDGE,"E4.5.0"),sQuery(id+"F0.wireOp",EDGE,"E4.6.0"),sQuery(id+"F0.wireOp",EDGE,"E4.7.0"),sQuery(id+"F0.wireOp",EDGE,"E4.8.0"),sQuery(id+"F0.wireOp",EDGE,"E4.9.0"),sQuery(id+"F0.wireOp",EDGE,"E4.10.0"),sQuery(id+"F0.wireOp",EDGE,"E4.11.0"),sQuery(id+"F0.wireOp",EDGE,"E4.12.0"),sQuery(id+"F0.wireOp",EDGE,"E4.13.0"),sQuery(id+"F0.wireOp",EDGE,"E17.trimOffspring")])],"isStart":false});
            var sketch = newSketch(context, id + "F4", { "sketchPlane" : qUnion([Q0])});
            skFitSpline(sketch, "E19", {"points": [v(-4.46, -7) * mm, v(-4.21, -6.46) * mm, v(-4, -5.96) * mm, v(-3.67, -5.74) * mm, v(-2.7, -5.74) * mm, v(-1.74, -5.78) * mm, v(-1.34, -5.6) * mm, v(-1.1, -5.28) * mm, v(-0.95, -4.8) * mm, v(-0.91, -3.73) * mm, v(-0.87, -1.33) * mm, v(-0.91, 4.09) * mm, v(-0.95, 5.38) * mm, v(-1.02, 5.56) * mm, v(-1.41, 5.52) * mm, v(-2.7, 5.1) * mm, v(-3.6, 4.41) * mm, v(-4.57, 3.7) * mm, v(-5.07, 3.48) * mm, v(-4.79, 2.94) * mm, v(-4.03, 1.76) * mm, v(-2.6, -0.36) * mm, v(-2.53, -0.68) * mm, v(-2.96, -1.65) * mm, v(-4.07, -2.51) * mm, v(-5.9, -2.87) * mm, v(-7.01, -2.58) * mm, v(-8.05, -1.76) * mm, v(-8.59, -0.68) * mm, v(-8.16, 0.4) * mm, v(-6.22, 2.98) * mm, v(-6.11, 3.26) * mm, v(-6.44, 3.34) * mm, v(-8.27, 3.77) * mm, v(-8.23, 4.16) * mm, v(-7.73, 4.8) * mm, v(-7.19, 4.7) * mm, v(-6.04, 4.48) * mm, v(-4.07, 5.63) * mm, v(-2.63, 6.5) * mm, v(-1.23, 6.74) * mm, v(-0.66, 6.89) * mm, v(-0.95, 7.28) * mm, v(-0.7, 7.96) * mm, v(-0.37, 8.07) * mm, v(0.3, 8.04) * mm, v(0.56, 7.53) * mm, v(0.38, 7.07) * mm, v(0.27, 6.92) * mm, v(0.88, 6.82) * mm, v(2.25, 6.53) * mm, v(3.79, 5.7) * mm, v(4.8, 4.91) * mm, v(5.37, 4.48) * mm, v(6.37, 4.6) * mm, v(7.34, 4.95) * mm, v(7.6, 4.7) * mm, v(8.06, 3.8) * mm, v(7.48, 3.59) * mm, v(5.87, 3.3) * mm, v(6.09, 2.87) * mm, v(8.38, -0.43) * mm, v(8.17, -1.47) * mm, v(7.34, -2.33) * mm, v(5.98, -2.94) * mm, v(4.61, -2.87) * mm, v(3.65, -2.48) * mm, v(2.9, -1.76) * mm, v(2.4, -0.93) * mm, v(2.28, -0.32) * mm, v(3.14, 0.93) * mm, v(4.04, 2.3) * mm, v(4.8, 3.26) * mm, v(4.8, 3.55) * mm, v(4.11, 3.84) * mm, v(3.22, 4.63) * mm, v(2.32, 5.13) * mm, v(1.13, 5.56) * mm, v(0.56, 5.56) * mm, v(0.6, 5.17) * mm, v(0.63, 3.01) * mm, v(0.7, -1.3) * mm, v(0.67, -4.84) * mm, v(0.95, -5.63) * mm, v(1.5, -5.78) * mm, v(2.96, -5.85) * mm, v(3.4, -5.78) * mm, v(3.65, -6.14) * mm, v(4, -7) * mm, v(3.72, -7.1) * mm, v(-3.5, -7.1) * mm, v(-4.46, -7) * mm]});
            skLineSegment(sketch, "E20", {"start": v(-7.8, -0.4) * mm, "end": v(-5.83, 2.58) * mm});
            skLineSegment(sketch, "E21", {"start": v(-5.83, 2.58) * mm, "end": v(-5.83, -0.36) * mm});
            skLineSegment(sketch, "E22", {"start": v(-5.83, -0.36) * mm, "end": v(-7.8, -0.4) * mm});
            skLineSegment(sketch, "E23", {"start": v(-5.36, 2.58) * mm, "end": v(-5.36, -0.4) * mm});
            skLineSegment(sketch, "E24", {"start": v(-5.36, -0.4) * mm, "end": v(-3.57, -0.4) * mm});
            skLineSegment(sketch, "E25", {"start": v(-3.57, -0.4) * mm, "end": v(-5.36, 2.58) * mm});
            skLineSegment(sketch, "E26", {"start": v(4.94, 2.58) * mm, "end": v(3.14, -0.4) * mm});
            skLineSegment(sketch, "E27", {"start": v(3.14, -0.4) * mm, "end": v(5.05, -0.4) * mm});
            skLineSegment(sketch, "E28", {"start": v(5.05, -0.4) * mm, "end": v(4.94, 2.58) * mm});
            skLineSegment(sketch, "E29", {"start": v(5.55, 2.58) * mm, "end": v(5.55, -0.4) * mm});
            skLineSegment(sketch, "E30", {"start": v(5.55, -0.4) * mm, "end": v(7.48, -0.4) * mm});
            skLineSegment(sketch, "E31", {"start": v(7.48, -0.4) * mm, "end": v(5.55, 2.58) * mm});
            skSolve(sketch);
        }
        {
            var Q0;
            Q0=makeQuery(id+"F4.imprint","IMPRINT",FACE,{"disambiguationData":[TD([[makeQuery(id+"F4.imprint","IMPRINT",EDGE,{"derivedFrom":sQuery(id+"F4.wireOp",EDGE,"E19")}),-1.0]])]});
            extrude(context, id + "F5", {"entities" : qUnion([Q0]), "operationType" : NewBodyOperationType.REMOVE, "oppositeDirection" : true, "depth" : 1 * mm, "offsetDistance" : 25 * mm});
        }
        {
            var Q0;
            Q0=makeQuery(id+"F1.opExtrude","CAP_FACE",FACE,{"disambiguationData":[OSD([sQuery(id+"F0.wireOp",EDGE,"E0"),sQuery(id+"F0.wireOp",EDGE,"E4.2.2"),sQuery(id+"F0.wireOp",EDGE,"E4.3.0"),sQuery(id+"F0.wireOp",EDGE,"E4.3.2"),sQuery(id+"F0.wireOp",EDGE,"E4.4.1"),sQuery(id+"F0.wireOp",EDGE,"E16.trimOffspring"),sQuery(id+"F0.wireOp",EDGE,"E18.trimOffspring")])],"isStart":false});
            var Q1;
            Q1=makeQuery(id+"F1.opExtrude","CAP_FACE",FACE,{"disambiguationData":[OSD([sQuery(id+"F0.wireOp",EDGE,"E0"),sQuery(id+"F0.wireOp",EDGE,"E4.3.2"),sQuery(id+"F0.wireOp",EDGE,"E4.4.0"),sQuery(id+"F0.wireOp",EDGE,"E4.4.2"),sQuery(id+"F0.wireOp",EDGE,"E4.5.1"),sQuery(id+"F0.wireOp",EDGE,"E15.trimOffspring"),sQuery(id+"F0.wireOp",EDGE,"E16.trimOffspring")])],"isStart":false});
            var Q2;
            Q2=makeQuery(id+"F1.opExtrude","CAP_FACE",FACE,{"disambiguationData":[OSD([sQuery(id+"F0.wireOp",EDGE,"E0"),sQuery(id+"F0.wireOp",EDGE,"E4.4.2"),sQuery(id+"F0.wireOp",EDGE,"E4.5.0"),sQuery(id+"F0.wireOp",EDGE,"E4.5.2"),sQuery(id+"F0.wireOp",EDGE,"E4.6.1"),sQuery(id+"F0.wireOp",EDGE,"E14.trimOffspring"),sQuery(id+"F0.wireOp",EDGE,"E15.trimOffspring")])],"isStart":false});
            var Q3;
            Q3=makeQuery(id+"F1.opExtrude","CAP_FACE",FACE,{"disambiguationData":[OSD([sQuery(id+"F0.wireOp",EDGE,"E0"),sQuery(id+"F0.wireOp",EDGE,"E4.5.2"),sQuery(id+"F0.wireOp",EDGE,"E4.6.0"),sQuery(id+"F0.wireOp",EDGE,"E4.6.2"),sQuery(id+"F0.wireOp",EDGE,"E4.7.1"),sQuery(id+"F0.wireOp",EDGE,"E13.trimOffspring"),sQuery(id+"F0.wireOp",EDGE,"E14.trimOffspring")])],"isStart":false});
            var Q4;
            Q4=makeQuery(id+"F1.opExtrude","CAP_FACE",FACE,{"disambiguationData":[OSD([sQuery(id+"F0.wireOp",EDGE,"E0"),sQuery(id+"F0.wireOp",EDGE,"E4.6.2"),sQuery(id+"F0.wireOp",EDGE,"E4.7.0"),sQuery(id+"F0.wireOp",EDGE,"E4.7.2"),sQuery(id+"F0.wireOp",EDGE,"E4.8.1"),sQuery(id+"F0.wireOp",EDGE,"E12.trimOffspring"),sQuery(id+"F0.wireOp",EDGE,"E13.trimOffspring")])],"isStart":false});
            var Q5;
            Q5=makeQuery(id+"F1.opExtrude","CAP_FACE",FACE,{"disambiguationData":[OSD([sQuery(id+"F0.wireOp",EDGE,"E0"),sQuery(id+"F0.wireOp",EDGE,"E4.7.2"),sQuery(id+"F0.wireOp",EDGE,"E4.8.0"),sQuery(id+"F0.wireOp",EDGE,"E4.8.2"),sQuery(id+"F0.wireOp",EDGE,"E4.9.1"),sQuery(id+"F0.wireOp",EDGE,"E11.trimOffspring"),sQuery(id+"F0.wireOp",EDGE,"E12.trimOffspring")])],"isStart":false});
            var Q6;
            Q6=makeQuery(id+"F1.opExtrude","CAP_FACE",FACE,{"disambiguationData":[OSD([sQuery(id+"F0.wireOp",EDGE,"E0"),sQuery(id+"F0.wireOp",EDGE,"E4.8.2"),sQuery(id+"F0.wireOp",EDGE,"E4.9.0"),sQuery(id+"F0.wireOp",EDGE,"E4.9.2"),sQuery(id+"F0.wireOp",EDGE,"E4.10.1"),sQuery(id+"F0.wireOp",EDGE,"E10.trimOffspring"),sQuery(id+"F0.wireOp",EDGE,"E11.trimOffspring")])],"isStart":false});
            var Q7;
            Q7=makeQuery(id+"F1.opExtrude","CAP_FACE",FACE,{"disambiguationData":[OSD([sQuery(id+"F0.wireOp",EDGE,"E0"),sQuery(id+"F0.wireOp",EDGE,"E4.9.2"),sQuery(id+"F0.wireOp",EDGE,"E4.10.0"),sQuery(id+"F0.wireOp",EDGE,"E4.10.2"),sQuery(id+"F0.wireOp",EDGE,"E4.11.1"),sQuery(id+"F0.wireOp",EDGE,"E9.trimOffspring"),sQuery(id+"F0.wireOp",EDGE,"E10.trimOffspring")])],"isStart":false});
            var Q8;
            Q8=makeQuery(id+"F1.opExtrude","CAP_FACE",FACE,{"disambiguationData":[OSD([sQuery(id+"F0.wireOp",EDGE,"E0"),sQuery(id+"F0.wireOp",EDGE,"E4.10.2"),sQuery(id+"F0.wireOp",EDGE,"E4.11.0"),sQuery(id+"F0.wireOp",EDGE,"E4.11.2"),sQuery(id+"F0.wireOp",EDGE,"E4.12.1"),sQuery(id+"F0.wireOp",EDGE,"E8.trimOffspring"),sQuery(id+"F0.wireOp",EDGE,"E9.trimOffspring")])],"isStart":false});
            var Q9;
            Q9=makeQuery(id+"F1.opExtrude","CAP_FACE",FACE,{"disambiguationData":[OSD([sQuery(id+"F0.wireOp",EDGE,"E0"),sQuery(id+"F0.wireOp",EDGE,"E4.11.2"),sQuery(id+"F0.wireOp",EDGE,"E4.12.0"),sQuery(id+"F0.wireOp",EDGE,"E4.12.2"),sQuery(id+"F0.wireOp",EDGE,"E4.13.1"),sQuery(id+"F0.wireOp",EDGE,"E7.trimOffspring"),sQuery(id+"F0.wireOp",EDGE,"E8.trimOffspring")])],"isStart":false});
            var Q10;
            Q10=makeQuery(id+"F1.opExtrude","CAP_FACE",FACE,{"disambiguationData":[OSD([sQuery(id+"F0.wireOp",EDGE,"E0"),sQuery(id+"F0.wireOp",EDGE,"E2"),sQuery(id+"F0.wireOp",EDGE,"E4.12.2"),sQuery(id+"F0.wireOp",EDGE,"E4.13.0"),sQuery(id+"F0.wireOp",EDGE,"E4.13.2"),sQuery(id+"F0.wireOp",EDGE,"E6.trimOffspring"),sQuery(id+"F0.wireOp",EDGE,"E7.trimOffspring")])],"isStart":false});
            var Q11;
            Q11=makeQuery(id+"F1.opExtrude","CAP_FACE",FACE,{"disambiguationData":[OSD([sQuery(id+"F0.wireOp",EDGE,"E0"),sQuery(id+"F0.wireOp",EDGE,"E1"),sQuery(id+"F0.wireOp",EDGE,"E3"),sQuery(id+"F0.wireOp",EDGE,"E4.1.1"),sQuery(id+"F0.wireOp",EDGE,"E4.13.2"),sQuery(id+"F0.wireOp",EDGE,"E5.trimOffspring"),sQuery(id+"F0.wireOp",EDGE,"E6.trimOffspring")])],"isStart":false});
            var Q12;
            Q12=makeQuery(id+"F1.opExtrude","CAP_FACE",FACE,{"disambiguationData":[OSD([sQuery(id+"F0.wireOp",EDGE,"E0"),sQuery(id+"F0.wireOp",EDGE,"E1"),sQuery(id+"F0.wireOp",EDGE,"E4.1.0"),sQuery(id+"F0.wireOp",EDGE,"E4.1.2"),sQuery(id+"F0.wireOp",EDGE,"E4.2.0"),sQuery(id+"F0.wireOp",EDGE,"E4.2.1"),sQuery(id+"F0.wireOp",EDGE,"E5.trimOffspring")])],"isStart":false});
            var Q13;
            Q13=makeQuery(id+"F1.opExtrude","CAP_FACE",FACE,{"disambiguationData":[OSD([sQuery(id+"F0.wireOp",EDGE,"E0"),sQuery(id+"F0.wireOp",EDGE,"E4.1.2"),sQuery(id+"F0.wireOp",EDGE,"E4.2.0"),sQuery(id+"F0.wireOp",EDGE,"E4.2.2"),sQuery(id+"F0.wireOp",EDGE,"E4.3.1"),sQuery(id+"F0.wireOp",EDGE,"E17.trimOffspring"),sQuery(id+"F0.wireOp",EDGE,"E18.trimOffspring")])],"isStart":false});
            fillet(context, id + "F6", {"entities" : qUnion([Q0, Q1, Q2, Q3, Q4, Q5, Q6, Q7, Q8, Q9, Q10, Q11, Q12, Q13]), "radius" : 2 * mm, "tangentPropagation" : true, "allowEdgeOverflow" : false});
        }
        {
            var Q0;
            {var subQ0=sQuery(id+"F0.wireOp",EDGE,"E0");var subQ1=makeQuery(id+"F0.imprint","INTERSECT",VERTEX,{"derivedFrom":[subQ0,sQuery(id+"F0.wireOp",EDGE,"E4.5.2")]});var subQ2=makeQuery(id+"F0.imprint","INTERSECT",VERTEX,{"derivedFrom":[subQ0,sQuery(id+"F0.wireOp",EDGE,"E4.6.1")]});Q0=makeQuery(id+"F2.opExtrude","CAP_EDGE",EDGE,{"disambiguationData":[OSD([subQ0]),TDD([makeQuery(id+"F0.imprint","IMPRINT",EDGE,{"disambiguationData":[TD([[subQ2,1.0]])],"derivedFrom":subQ0}),makeQuery(id+"F0.imprint","IMPRINT",EDGE,{"disambiguationData":[TD([[subQ1,1.0]])],"derivedFrom":subQ0}),makeQuery(id+"F0.imprint","IMPRINT",EDGE,{"disambiguationData":[TD([[subQ1,-1.0]])],"derivedFrom":subQ0})])],"isStart":false});}
            var Q1;
            Q1=makeQuery(id+"F2.opExtrude","CAP_EDGE",EDGE,{"disambiguationData":[OSD([sQuery(id+"F0.wireOp",EDGE,"E4.5.0")])],"isStart":false});
            var Q2;
            {var subQ0=sQuery(id+"F0.wireOp",EDGE,"E0");var subQ1=makeQuery(id+"F0.imprint","INTERSECT",VERTEX,{"derivedFrom":[subQ0,sQuery(id+"F0.wireOp",EDGE,"E4.4.2")]});var subQ2=makeQuery(id+"F0.imprint","INTERSECT",VERTEX,{"derivedFrom":[subQ0,sQuery(id+"F0.wireOp",EDGE,"E4.5.1")]});Q2=makeQuery(id+"F2.opExtrude","CAP_EDGE",EDGE,{"disambiguationData":[OSD([subQ0]),TDD([makeQuery(id+"F0.imprint","IMPRINT",EDGE,{"disambiguationData":[TD([[subQ2,1.0]])],"derivedFrom":subQ0}),makeQuery(id+"F0.imprint","IMPRINT",EDGE,{"disambiguationData":[TD([[subQ1,1.0]])],"derivedFrom":subQ0}),makeQuery(id+"F0.imprint","IMPRINT",EDGE,{"disambiguationData":[TD([[subQ1,-1.0]])],"derivedFrom":subQ0})])],"isStart":false});}
            var Q3;
            {var subQ0=sQuery(id+"F0.wireOp",EDGE,"E0");var subQ1=makeQuery(id+"F0.imprint","INTERSECT",VERTEX,{"derivedFrom":[subQ0,sQuery(id+"F0.wireOp",EDGE,"E4.3.2")]});var subQ2=makeQuery(id+"F0.imprint","INTERSECT",VERTEX,{"derivedFrom":[subQ0,sQuery(id+"F0.wireOp",EDGE,"E4.4.1")]});Q3=makeQuery(id+"F2.opExtrude","CAP_EDGE",EDGE,{"disambiguationData":[OSD([subQ0]),TDD([makeQuery(id+"F0.imprint","IMPRINT",EDGE,{"disambiguationData":[TD([[subQ2,1.0]])],"derivedFrom":subQ0}),makeQuery(id+"F0.imprint","IMPRINT",EDGE,{"disambiguationData":[TD([[subQ1,1.0]])],"derivedFrom":subQ0}),makeQuery(id+"F0.imprint","IMPRINT",EDGE,{"disambiguationData":[TD([[subQ1,-1.0]])],"derivedFrom":subQ0})])],"isStart":false});}
            var Q4;
            {var subQ0=sQuery(id+"F0.wireOp",EDGE,"E0");var subQ1=makeQuery(id+"F0.imprint","INTERSECT",VERTEX,{"derivedFrom":[subQ0,sQuery(id+"F0.wireOp",EDGE,"E4.2.2")]});var subQ2=makeQuery(id+"F0.imprint","INTERSECT",VERTEX,{"derivedFrom":[subQ0,sQuery(id+"F0.wireOp",EDGE,"E4.3.1")]});Q4=makeQuery(id+"F2.opExtrude","CAP_EDGE",EDGE,{"disambiguationData":[OSD([subQ0]),TDD([makeQuery(id+"F0.imprint","IMPRINT",EDGE,{"disambiguationData":[TD([[subQ2,1.0]])],"derivedFrom":subQ0}),makeQuery(id+"F0.imprint","IMPRINT",EDGE,{"disambiguationData":[TD([[subQ1,1.0]])],"derivedFrom":subQ0}),makeQuery(id+"F0.imprint","IMPRINT",EDGE,{"disambiguationData":[TD([[subQ1,-1.0]])],"derivedFrom":subQ0})])],"isStart":false});}
            var Q5;
            Q5=makeQuery(id+"F2.opExtrude","CAP_EDGE",EDGE,{"disambiguationData":[OSD([sQuery(id+"F0.wireOp",EDGE,"E4.3.0")])],"isStart":false});
            var Q6;
            Q6=makeQuery(id+"F2.opExtrude","CAP_EDGE",EDGE,{"disambiguationData":[OSD([sQuery(id+"F0.wireOp",EDGE,"E17.trimOffspring")])],"isStart":false});
            var Q7;
            {var subQ0=sQuery(id+"F0.wireOp",EDGE,"E0");var subQ1=makeQuery(id+"F0.imprint","INTERSECT",VERTEX,{"derivedFrom":[subQ0,sQuery(id+"F0.wireOp",EDGE,"E4.1.2")]});var subQ2=makeQuery(id+"F0.imprint","INTERSECT",VERTEX,{"derivedFrom":[subQ0,sQuery(id+"F0.wireOp",EDGE,"E4.2.1")]});Q7=makeQuery(id+"F2.opExtrude","CAP_EDGE",EDGE,{"disambiguationData":[OSD([subQ0]),TDD([makeQuery(id+"F0.imprint","IMPRINT",EDGE,{"disambiguationData":[TD([[subQ2,1.0]])],"derivedFrom":subQ0}),makeQuery(id+"F0.imprint","IMPRINT",EDGE,{"disambiguationData":[TD([[subQ1,1.0]])],"derivedFrom":subQ0}),makeQuery(id+"F0.imprint","IMPRINT",EDGE,{"disambiguationData":[TD([[subQ1,-1.0]])],"derivedFrom":subQ0})])],"isStart":false});}
            var Q8;
            Q8=makeQuery(id+"F2.opExtrude","CAP_EDGE",EDGE,{"disambiguationData":[OSD([sQuery(id+"F0.wireOp",EDGE,"E4.6.0")])],"isStart":false});
            var Q9;
            {var subQ0=sQuery(id+"F0.wireOp",EDGE,"E0");var subQ1=makeQuery(id+"F0.imprint","INTERSECT",VERTEX,{"derivedFrom":[subQ0,sQuery(id+"F0.wireOp",EDGE,"E4.6.2")]});var subQ2=makeQuery(id+"F0.imprint","INTERSECT",VERTEX,{"derivedFrom":[subQ0,sQuery(id+"F0.wireOp",EDGE,"E4.7.1")]});Q9=makeQuery(id+"F2.opExtrude","CAP_EDGE",EDGE,{"disambiguationData":[OSD([subQ0]),TDD([makeQuery(id+"F0.imprint","IMPRINT",EDGE,{"disambiguationData":[TD([[subQ2,1.0]])],"derivedFrom":subQ0}),makeQuery(id+"F0.imprint","IMPRINT",EDGE,{"disambiguationData":[TD([[subQ1,1.0]])],"derivedFrom":subQ0}),makeQuery(id+"F0.imprint","IMPRINT",EDGE,{"disambiguationData":[TD([[subQ1,-1.0]])],"derivedFrom":subQ0})])],"isStart":false});}
            var Q10;
            Q10=makeQuery(id+"F2.opExtrude","CAP_EDGE",EDGE,{"disambiguationData":[OSD([sQuery(id+"F0.wireOp",EDGE,"E4.7.0")])],"isStart":false});
            var Q11;
            {var subQ0=sQuery(id+"F0.wireOp",EDGE,"E0");var subQ1=makeQuery(id+"F0.imprint","INTERSECT",VERTEX,{"derivedFrom":[subQ0,sQuery(id+"F0.wireOp",EDGE,"E4.7.2")]});var subQ2=makeQuery(id+"F0.imprint","INTERSECT",VERTEX,{"derivedFrom":[subQ0,sQuery(id+"F0.wireOp",EDGE,"E4.8.1")]});Q11=makeQuery(id+"F2.opExtrude","CAP_EDGE",EDGE,{"disambiguationData":[OSD([subQ0]),TDD([makeQuery(id+"F0.imprint","IMPRINT",EDGE,{"disambiguationData":[TD([[subQ2,1.0]])],"derivedFrom":subQ0}),makeQuery(id+"F0.imprint","IMPRINT",EDGE,{"disambiguationData":[TD([[subQ1,1.0]])],"derivedFrom":subQ0}),makeQuery(id+"F0.imprint","IMPRINT",EDGE,{"disambiguationData":[TD([[subQ1,-1.0]])],"derivedFrom":subQ0})])],"isStart":false});}
            var Q12;
            Q12=makeQuery(id+"F2.opExtrude","CAP_EDGE",EDGE,{"disambiguationData":[OSD([sQuery(id+"F0.wireOp",EDGE,"E4.8.0")])],"isStart":false});
            var Q13;
            {var subQ0=sQuery(id+"F0.wireOp",EDGE,"E0");var subQ1=makeQuery(id+"F0.imprint","INTERSECT",VERTEX,{"derivedFrom":[subQ0,sQuery(id+"F0.wireOp",EDGE,"E4.8.2")]});var subQ2=makeQuery(id+"F0.imprint","INTERSECT",VERTEX,{"derivedFrom":[subQ0,sQuery(id+"F0.wireOp",EDGE,"E4.9.1")]});Q13=makeQuery(id+"F2.opExtrude","CAP_EDGE",EDGE,{"disambiguationData":[OSD([subQ0]),TDD([makeQuery(id+"F0.imprint","IMPRINT",EDGE,{"disambiguationData":[TD([[subQ2,1.0]])],"derivedFrom":subQ0}),makeQuery(id+"F0.imprint","IMPRINT",EDGE,{"disambiguationData":[TD([[subQ1,1.0]])],"derivedFrom":subQ0}),makeQuery(id+"F0.imprint","IMPRINT",EDGE,{"disambiguationData":[TD([[subQ1,-1.0]])],"derivedFrom":subQ0})])],"isStart":false});}
            var Q14;
            Q14=makeQuery(id+"F2.opExtrude","CAP_EDGE",EDGE,{"disambiguationData":[OSD([sQuery(id+"F0.wireOp",EDGE,"E4.9.0")])],"isStart":false});
            var Q15;
            {var subQ0=sQuery(id+"F0.wireOp",EDGE,"E0");var subQ1=makeQuery(id+"F0.imprint","INTERSECT",VERTEX,{"derivedFrom":[subQ0,sQuery(id+"F0.wireOp",EDGE,"E4.10.1")]});Q15=makeQuery(id+"F2.opExtrude","CAP_EDGE",EDGE,{"disambiguationData":[OSD([subQ0]),TDD([makeQuery(id+"F0.imprint","IMPRINT",EDGE,{"disambiguationData":[TD([[subQ1,1.0]])],"derivedFrom":subQ0}),makeQuery(id+"F0.imprint","IMPRINT",EDGE,{"disambiguationData":[TD([[subQ1,-1.0]])],"derivedFrom":subQ0})])],"isStart":false});}
            var Q16;
            Q16=makeQuery(id+"F2.opExtrude","CAP_EDGE",EDGE,{"disambiguationData":[OSD([sQuery(id+"F0.wireOp",EDGE,"E4.10.0")])],"isStart":false});
            var Q17;
            {var subQ0=sQuery(id+"F0.wireOp",EDGE,"E0");var subQ1=makeQuery(id+"F0.imprint","INTERSECT",VERTEX,{"derivedFrom":[subQ0,sQuery(id+"F0.wireOp",EDGE,"E4.10.2")]});var subQ2=makeQuery(id+"F0.imprint","INTERSECT",VERTEX,{"derivedFrom":[subQ0,sQuery(id+"F0.wireOp",EDGE,"E4.11.1")]});Q17=makeQuery(id+"F2.opExtrude","CAP_EDGE",EDGE,{"disambiguationData":[OSD([subQ0]),TDD([makeQuery(id+"F0.imprint","IMPRINT",EDGE,{"disambiguationData":[TD([[subQ2,1.0]])],"derivedFrom":subQ0}),makeQuery(id+"F0.imprint","IMPRINT",EDGE,{"disambiguationData":[TD([[subQ1,1.0]])],"derivedFrom":subQ0}),makeQuery(id+"F0.imprint","IMPRINT",EDGE,{"disambiguationData":[TD([[subQ1,-1.0]])],"derivedFrom":subQ0})])],"isStart":false});}
            var Q18;
            Q18=makeQuery(id+"F2.opExtrude","CAP_EDGE",EDGE,{"disambiguationData":[OSD([sQuery(id+"F0.wireOp",EDGE,"E4.11.0")])],"isStart":false});
            var Q19;
            {var subQ0=sQuery(id+"F0.wireOp",EDGE,"E0");var subQ1=makeQuery(id+"F0.imprint","INTERSECT",VERTEX,{"derivedFrom":[subQ0,sQuery(id+"F0.wireOp",EDGE,"E4.11.2")]});var subQ2=makeQuery(id+"F0.imprint","INTERSECT",VERTEX,{"derivedFrom":[subQ0,sQuery(id+"F0.wireOp",EDGE,"E4.12.1")]});Q19=makeQuery(id+"F2.opExtrude","CAP_EDGE",EDGE,{"disambiguationData":[OSD([subQ0]),TDD([makeQuery(id+"F0.imprint","IMPRINT",EDGE,{"disambiguationData":[TD([[subQ2,1.0]])],"derivedFrom":subQ0}),makeQuery(id+"F0.imprint","IMPRINT",EDGE,{"disambiguationData":[TD([[subQ1,1.0]])],"derivedFrom":subQ0}),makeQuery(id+"F0.imprint","IMPRINT",EDGE,{"disambiguationData":[TD([[subQ1,-1.0]])],"derivedFrom":subQ0})])],"isStart":false});}
            var Q20;
            Q20=makeQuery(id+"F2.opExtrude","CAP_EDGE",EDGE,{"disambiguationData":[OSD([sQuery(id+"F0.wireOp",EDGE,"E4.12.0")])],"isStart":false});
            var Q21;
            {var subQ0=sQuery(id+"F0.wireOp",EDGE,"E0");var subQ1=makeQuery(id+"F0.imprint","INTERSECT",VERTEX,{"derivedFrom":[subQ0,sQuery(id+"F0.wireOp",EDGE,"E4.12.2")]});var subQ2=makeQuery(id+"F0.imprint","INTERSECT",VERTEX,{"derivedFrom":[subQ0,sQuery(id+"F0.wireOp",EDGE,"E4.13.1")]});Q21=makeQuery(id+"F2.opExtrude","CAP_EDGE",EDGE,{"disambiguationData":[OSD([subQ0]),TDD([makeQuery(id+"F0.imprint","IMPRINT",EDGE,{"disambiguationData":[TD([[subQ2,1.0]])],"derivedFrom":subQ0}),makeQuery(id+"F0.imprint","IMPRINT",EDGE,{"disambiguationData":[TD([[subQ1,1.0]])],"derivedFrom":subQ0}),makeQuery(id+"F0.imprint","IMPRINT",EDGE,{"disambiguationData":[TD([[subQ1,-1.0]])],"derivedFrom":subQ0})])],"isStart":false});}
            var Q22;
            {var subQ0=sQuery(id+"F0.wireOp",EDGE,"E0");var subQ1=makeQuery(id+"F0.imprint","INTERSECT",VERTEX,{"derivedFrom":[subQ0,sQuery(id+"F0.wireOp",EDGE,"E4.13.2")]});var subQ2=makeQuery(id+"F0.imprint","INTERSECT",VERTEX,{"derivedFrom":[subQ0,sQuery(id+"F0.wireOp",EDGE,"E2")]});Q22=makeQuery(id+"F2.opExtrude","CAP_EDGE",EDGE,{"disambiguationData":[OSD([subQ0]),TDD([makeQuery(id+"F0.imprint","IMPRINT",EDGE,{"disambiguationData":[TD([[subQ2,1.0]])],"derivedFrom":subQ0}),makeQuery(id+"F0.imprint","IMPRINT",EDGE,{"disambiguationData":[TD([[subQ2,-1.0]])],"derivedFrom":subQ0}),makeQuery(id+"F0.imprint","IMPRINT",EDGE,{"disambiguationData":[TD([[subQ1,-1.0]])],"derivedFrom":subQ0})])],"isStart":false});}
            var Q23;
            Q23=makeQuery(id+"F2.opExtrude","CAP_EDGE",EDGE,{"disambiguationData":[OSD([sQuery(id+"F0.wireOp",EDGE,"E3")])],"isStart":false});
            var Q24;
            {var subQ0=sQuery(id+"F0.wireOp",EDGE,"E0");var subQ1=makeQuery(id+"F0.imprint","INTERSECT",VERTEX,{"derivedFrom":[subQ0,sQuery(id+"F0.wireOp",EDGE,"E1")]});var subQ2=makeQuery(id+"F0.imprint","INTERSECT",VERTEX,{"derivedFrom":[subQ0,sQuery(id+"F0.wireOp",EDGE,"E4.1.1")]});Q24=makeQuery(id+"F2.opExtrude","CAP_EDGE",EDGE,{"disambiguationData":[OSD([subQ0]),TDD([makeQuery(id+"F0.imprint","IMPRINT",EDGE,{"disambiguationData":[TD([[subQ2,1.0]])],"derivedFrom":subQ0}),makeQuery(id+"F0.imprint","IMPRINT",EDGE,{"disambiguationData":[TD([[subQ1,1.0]])],"derivedFrom":subQ0}),makeQuery(id+"F0.imprint","IMPRINT",EDGE,{"disambiguationData":[TD([[subQ1,-1.0]])],"derivedFrom":subQ0})])],"isStart":false});}
            var Q25;
            Q25=makeQuery(id+"F2.opExtrude","CAP_EDGE",EDGE,{"disambiguationData":[OSD([sQuery(id+"F0.wireOp",EDGE,"E4.1.0")])],"isStart":false});
            var Q26;
            Q26=makeQuery(id+"F2.opExtrude","CAP_EDGE",EDGE,{"disambiguationData":[OSD([sQuery(id+"F0.wireOp",EDGE,"E4.13.0")])],"isStart":false});
            var Q27;
            Q27=makeQuery(id+"F2.opExtrude","CAP_EDGE",EDGE,{"disambiguationData":[OSD([sQuery(id+"F0.wireOp",EDGE,"E4.4.0")])],"isStart":false});
            fillet(context, id + "F7", {"entities" : qUnion([Q0, Q1, Q2, Q3, Q4, Q5, Q6, Q7, Q8, Q9, Q10, Q11, Q12, Q13, Q14, Q15, Q16, Q17, Q18, Q19, Q20, Q21, Q22, Q23, Q24, Q25, Q26, Q27]), "radius" : 1 * mm, "tangentPropagation" : true, "allowEdgeOverflow" : false});
        }
        {
            var Q0;
            Q0=makeQuery(id+"F5.boolean.opBoolean","COPY",FACE,{"derivedFrom":makeQuery(id+"F5.opExtrude","CAP_FACE",FACE,{"disambiguationData":[OSD([sQuery(id+"F4.wireOp",EDGE,"E19"),sQuery(id+"F4.wireOp",EDGE,"E20"),sQuery(id+"F4.wireOp",EDGE,"E21"),sQuery(id+"F4.wireOp",EDGE,"E22"),sQuery(id+"F4.wireOp",EDGE,"E23"),sQuery(id+"F4.wireOp",EDGE,"E24"),sQuery(id+"F4.wireOp",EDGE,"E25"),sQuery(id+"F4.wireOp",EDGE,"E26"),sQuery(id+"F4.wireOp",EDGE,"E27"),sQuery(id+"F4.wireOp",EDGE,"E28"),sQuery(id+"F4.wireOp",EDGE,"E29"),sQuery(id+"F4.wireOp",EDGE,"E30"),sQuery(id+"F4.wireOp",EDGE,"E31")])],"isStart":false})});
            fillet(context, id + "F8", {"entities" : qUnion([Q0]), "radius" : 0.2 * mm, "tangentPropagation" : true, "allowEdgeOverflow" : false});
        }
    });
